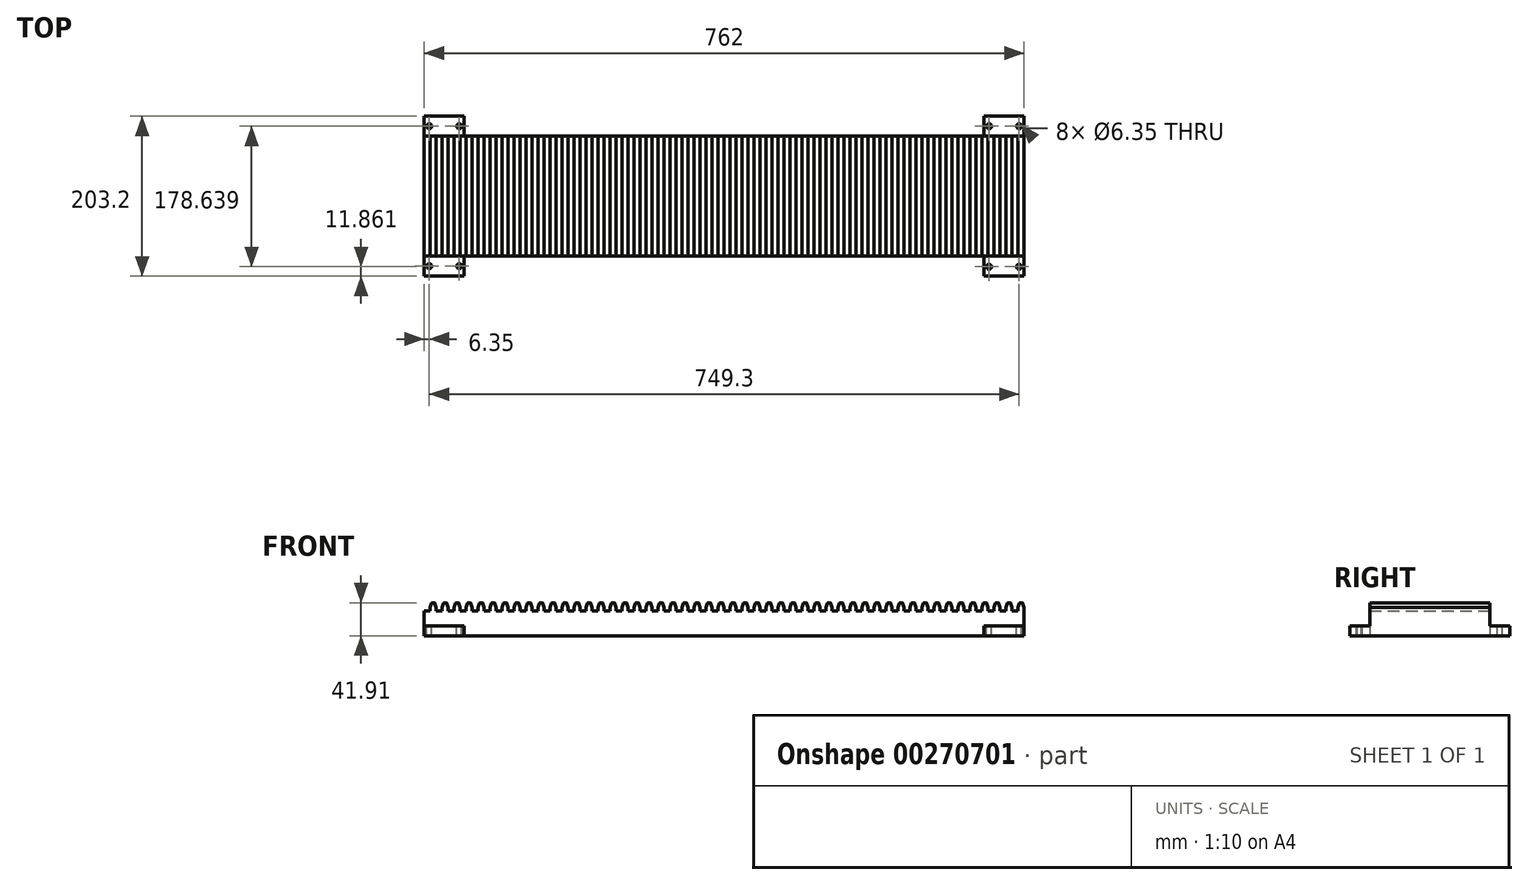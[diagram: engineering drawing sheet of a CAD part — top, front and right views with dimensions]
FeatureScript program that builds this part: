
annotation { "Feature Type Name" : "Feature", "Feature Type Description" : "" }
export const myFeature = defineFeature(function(context is Context, id is Id, definition is map)
    precondition{}
    {
        {
            var Q0;
            Q0=qCreatedBy(makeId("Front.planeOp"),FACE);
            var sketch = newSketch(context, id + "F0", { "sketchPlane" : qUnion([Q0])});
            skLineSegment(sketch, "E0.bottom", {"start": v(0, 0) * mm, "end": v(762, 0) * mm});
            skLineSegment(sketch, "E0.top", {"start": v(0, 31.75) * mm, "end": v(762, 31.75) * mm});
            skLineSegment(sketch, "E0.left", {"start": v(0, 0) * mm, "end": v(0, 31.75) * mm});
            skLineSegment(sketch, "E0.right", {"start": v(762, 0) * mm, "end": v(762, 31.75) * mm});
            skPoint(sketch, "E1.centerSnap0", {"position": v(11.43, 41.91) * mm});
            skPoint(sketch, "E2", {"position": v(7.62, 35.71) * mm});
            skPoint(sketch, "E3", {"position": v(15.24, 35.71) * mm});
            skLineSegment(sketch, "E4", {"start": v(7.62, 31.75) * mm, "end": v(7.62, 35.71) * mm});
            skPoint(sketch, "E5", {"position": v(7.62, 41.91) * mm});
            skLineSegment(sketch, "E6", {"start": v(15.24, 35.71) * mm, "end": v(15.24, 31.75) * mm});
            skLineSegment(sketch, "E7", {"start": v(10, 41.91) * mm, "end": v(11.43, 41.91) * mm});
            skLineSegment(sketch, "E8", {"start": v(12.87, 41.91) * mm, "end": v(11.43, 41.91) * mm});
            skLineSegment(sketch, "E9", {"start": v(7.62, 35.71) * mm, "end": v(9.39, 41.46) * mm});
            skLineSegment(sketch, "E10", {"start": v(15.24, 35.71) * mm, "end": v(13.47, 41.46) * mm});
            skPoint(sketch, "E11.start.orphan", {"position": v(15.24, 41.91) * mm});
            skPoint(sketch, "E12.visualSharp", {"position": v(9.52, 41.91) * mm});
            skArc(sketch, "E12.filletArc", {"start": v(10, 41.91) * mm, "mid": v(9.62, 41.79) * mm, "end": v(9.39, 41.46) * mm});
            skPoint(sketch, "E13.visualSharp", {"position": v(13.33, 41.91) * mm});
            skArc(sketch, "E13.filletArc", {"start": v(13.47, 41.46) * mm, "mid": v(13.24, 41.79) * mm, "end": v(12.87, 41.91) * mm});
            skLineSegment(sketch, "E14.1.0.0", {"start": v(22.86, 31.75) * mm, "end": v(22.86, 35.71) * mm});
            skLineSegment(sketch, "E14.1.0.1", {"start": v(22.86, 35.71) * mm, "end": v(24.63, 41.46) * mm});
            skArc(sketch, "E14.1.0.2", {"start": v(25.23, 41.91) * mm, "mid": v(24.86, 41.79) * mm, "end": v(24.63, 41.46) * mm});
            skLineSegment(sketch, "E14.1.0.3", {"start": v(25.23, 41.91) * mm, "end": v(26.67, 41.91) * mm});
            skLineSegment(sketch, "E14.1.0.4", {"start": v(28.1, 41.91) * mm, "end": v(26.67, 41.91) * mm});
            skArc(sketch, "E14.1.0.5", {"start": v(28.71, 41.46) * mm, "mid": v(28.48, 41.79) * mm, "end": v(28.1, 41.91) * mm});
            skLineSegment(sketch, "E14.1.0.6", {"start": v(30.48, 35.71) * mm, "end": v(28.71, 41.46) * mm});
            skLineSegment(sketch, "E14.1.0.7", {"start": v(30.48, 35.71) * mm, "end": v(30.48, 31.75) * mm});
            skLineSegment(sketch, "E14.2.0.0", {"start": v(38.1, 31.75) * mm, "end": v(38.1, 35.71) * mm});
            skLineSegment(sketch, "E14.2.0.1", {"start": v(38.1, 35.71) * mm, "end": v(39.87, 41.46) * mm});
            skArc(sketch, "E14.2.0.2", {"start": v(40.47, 41.91) * mm, "mid": v(40.1, 41.79) * mm, "end": v(39.87, 41.46) * mm});
            skLineSegment(sketch, "E14.2.0.3", {"start": v(40.47, 41.91) * mm, "end": v(41.9, 41.91) * mm});
            skLineSegment(sketch, "E14.2.0.4", {"start": v(43.35, 41.91) * mm, "end": v(41.9, 41.91) * mm});
            skArc(sketch, "E14.2.0.5", {"start": v(43.95, 41.46) * mm, "mid": v(43.72, 41.79) * mm, "end": v(43.35, 41.91) * mm});
            skLineSegment(sketch, "E14.2.0.6", {"start": v(45.72, 35.71) * mm, "end": v(43.95, 41.46) * mm});
            skLineSegment(sketch, "E14.2.0.7", {"start": v(45.72, 35.71) * mm, "end": v(45.72, 31.75) * mm});
            skLineSegment(sketch, "E14.3.0.0", {"start": v(53.34, 31.75) * mm, "end": v(53.34, 35.71) * mm});
            skLineSegment(sketch, "E14.3.0.1", {"start": v(53.34, 35.71) * mm, "end": v(55.1, 41.46) * mm});
            skArc(sketch, "E14.3.0.2", {"start": v(55.71, 41.91) * mm, "mid": v(55.34, 41.79) * mm, "end": v(55.1, 41.46) * mm});
            skLineSegment(sketch, "E14.3.0.3", {"start": v(55.71, 41.91) * mm, "end": v(57.15, 41.91) * mm});
            skLineSegment(sketch, "E14.3.0.4", {"start": v(58.59, 41.91) * mm, "end": v(57.15, 41.91) * mm});
            skArc(sketch, "E14.3.0.5", {"start": v(59.2, 41.46) * mm, "mid": v(58.96, 41.79) * mm, "end": v(58.59, 41.91) * mm});
            skLineSegment(sketch, "E14.3.0.6", {"start": v(60.96, 35.71) * mm, "end": v(59.2, 41.46) * mm});
            skLineSegment(sketch, "E14.3.0.7", {"start": v(60.96, 35.71) * mm, "end": v(60.96, 31.75) * mm});
            skLineSegment(sketch, "E14.4.0.0", {"start": v(68.58, 31.75) * mm, "end": v(68.58, 35.71) * mm});
            skLineSegment(sketch, "E14.4.0.1", {"start": v(68.58, 35.71) * mm, "end": v(70.35, 41.46) * mm});
            skArc(sketch, "E14.4.0.2", {"start": v(70.95, 41.91) * mm, "mid": v(70.58, 41.79) * mm, "end": v(70.35, 41.46) * mm});
            skLineSegment(sketch, "E14.4.0.3", {"start": v(70.95, 41.91) * mm, "end": v(72.39, 41.91) * mm});
            skLineSegment(sketch, "E14.4.0.4", {"start": v(73.83, 41.91) * mm, "end": v(72.39, 41.91) * mm});
            skArc(sketch, "E14.4.0.5", {"start": v(74.43, 41.46) * mm, "mid": v(74.2, 41.79) * mm, "end": v(73.83, 41.91) * mm});
            skLineSegment(sketch, "E14.4.0.6", {"start": v(76.2, 35.71) * mm, "end": v(74.43, 41.46) * mm});
            skLineSegment(sketch, "E14.4.0.7", {"start": v(76.2, 35.71) * mm, "end": v(76.2, 31.75) * mm});
            skLineSegment(sketch, "E14.5.0.0", {"start": v(83.82, 31.75) * mm, "end": v(83.82, 35.71) * mm});
            skLineSegment(sketch, "E14.5.0.1", {"start": v(83.82, 35.71) * mm, "end": v(85.59, 41.46) * mm});
            skArc(sketch, "E14.5.0.2", {"start": v(86.2, 41.91) * mm, "mid": v(85.82, 41.79) * mm, "end": v(85.59, 41.46) * mm});
            skLineSegment(sketch, "E14.5.0.3", {"start": v(86.2, 41.91) * mm, "end": v(87.63, 41.91) * mm});
            skLineSegment(sketch, "E14.5.0.4", {"start": v(89.07, 41.91) * mm, "end": v(87.63, 41.91) * mm});
            skArc(sketch, "E14.5.0.5", {"start": v(89.67, 41.46) * mm, "mid": v(89.44, 41.79) * mm, "end": v(89.07, 41.91) * mm});
            skLineSegment(sketch, "E14.5.0.6", {"start": v(91.44, 35.71) * mm, "end": v(89.67, 41.46) * mm});
            skLineSegment(sketch, "E14.5.0.7", {"start": v(91.44, 35.71) * mm, "end": v(91.44, 31.75) * mm});
            skLineSegment(sketch, "E14.6.0.0", {"start": v(99.06, 31.75) * mm, "end": v(99.06, 35.71) * mm});
            skLineSegment(sketch, "E14.6.0.1", {"start": v(99.06, 35.71) * mm, "end": v(100.83, 41.46) * mm});
            skArc(sketch, "E14.6.0.2", {"start": v(101.43, 41.91) * mm, "mid": v(101.06, 41.79) * mm, "end": v(100.83, 41.46) * mm});
            skLineSegment(sketch, "E14.6.0.3", {"start": v(101.43, 41.91) * mm, "end": v(102.87, 41.91) * mm});
            skLineSegment(sketch, "E14.6.0.4", {"start": v(104.3, 41.91) * mm, "end": v(102.87, 41.91) * mm});
            skArc(sketch, "E14.6.0.5", {"start": v(104.91, 41.46) * mm, "mid": v(104.68, 41.79) * mm, "end": v(104.3, 41.91) * mm});
            skLineSegment(sketch, "E14.6.0.6", {"start": v(106.68, 35.71) * mm, "end": v(104.91, 41.46) * mm});
            skLineSegment(sketch, "E14.6.0.7", {"start": v(106.68, 35.71) * mm, "end": v(106.68, 31.75) * mm});
            skLineSegment(sketch, "E14.7.0.0", {"start": v(114.3, 31.75) * mm, "end": v(114.3, 35.71) * mm});
            skLineSegment(sketch, "E14.7.0.1", {"start": v(114.3, 35.71) * mm, "end": v(116.07, 41.46) * mm});
            skArc(sketch, "E14.7.0.2", {"start": v(116.67, 41.91) * mm, "mid": v(116.3, 41.79) * mm, "end": v(116.07, 41.46) * mm});
            skLineSegment(sketch, "E14.7.0.3", {"start": v(116.67, 41.91) * mm, "end": v(118.11, 41.91) * mm});
            skLineSegment(sketch, "E14.7.0.4", {"start": v(119.55, 41.91) * mm, "end": v(118.1, 41.91) * mm});
            skArc(sketch, "E14.7.0.5", {"start": v(120.15, 41.46) * mm, "mid": v(119.92, 41.79) * mm, "end": v(119.55, 41.91) * mm});
            skLineSegment(sketch, "E14.7.0.6", {"start": v(121.92, 35.71) * mm, "end": v(120.15, 41.46) * mm});
            skLineSegment(sketch, "E14.7.0.7", {"start": v(121.92, 35.71) * mm, "end": v(121.92, 31.75) * mm});
            skLineSegment(sketch, "E14.8.0.0", {"start": v(129.54, 31.75) * mm, "end": v(129.54, 35.71) * mm});
            skLineSegment(sketch, "E14.8.0.1", {"start": v(129.54, 35.71) * mm, "end": v(131.3, 41.46) * mm});
            skArc(sketch, "E14.8.0.2", {"start": v(131.91, 41.91) * mm, "mid": v(131.54, 41.79) * mm, "end": v(131.3, 41.46) * mm});
            skLineSegment(sketch, "E14.8.0.3", {"start": v(131.91, 41.91) * mm, "end": v(133.35, 41.91) * mm});
            skLineSegment(sketch, "E14.8.0.4", {"start": v(134.79, 41.91) * mm, "end": v(133.35, 41.91) * mm});
            skArc(sketch, "E14.8.0.5", {"start": v(135.4, 41.46) * mm, "mid": v(135.16, 41.79) * mm, "end": v(134.79, 41.91) * mm});
            skLineSegment(sketch, "E14.8.0.6", {"start": v(137.16, 35.71) * mm, "end": v(135.4, 41.46) * mm});
            skLineSegment(sketch, "E14.8.0.7", {"start": v(137.16, 35.71) * mm, "end": v(137.16, 31.75) * mm});
            skLineSegment(sketch, "E14.9.0.0", {"start": v(144.78, 31.75) * mm, "end": v(144.78, 35.71) * mm});
            skLineSegment(sketch, "E14.9.0.1", {"start": v(144.78, 35.71) * mm, "end": v(146.55, 41.46) * mm});
            skArc(sketch, "E14.9.0.2", {"start": v(147.15, 41.91) * mm, "mid": v(146.78, 41.79) * mm, "end": v(146.55, 41.46) * mm});
            skLineSegment(sketch, "E14.9.0.3", {"start": v(147.15, 41.91) * mm, "end": v(148.6, 41.91) * mm});
            skLineSegment(sketch, "E14.9.0.4", {"start": v(150.03, 41.91) * mm, "end": v(148.6, 41.91) * mm});
            skArc(sketch, "E14.9.0.5", {"start": v(150.63, 41.46) * mm, "mid": v(150.4, 41.79) * mm, "end": v(150.03, 41.91) * mm});
            skLineSegment(sketch, "E14.9.0.6", {"start": v(152.4, 35.71) * mm, "end": v(150.63, 41.46) * mm});
            skLineSegment(sketch, "E14.9.0.7", {"start": v(152.4, 35.71) * mm, "end": v(152.4, 31.75) * mm});
            skLineSegment(sketch, "E14.10.0.0", {"start": v(160.02, 31.75) * mm, "end": v(160.02, 35.71) * mm});
            skLineSegment(sketch, "E14.10.0.1", {"start": v(160.02, 35.71) * mm, "end": v(161.79, 41.46) * mm});
            skArc(sketch, "E14.10.0.2", {"start": v(162.4, 41.91) * mm, "mid": v(162.02, 41.79) * mm, "end": v(161.79, 41.46) * mm});
            skLineSegment(sketch, "E14.10.0.3", {"start": v(162.4, 41.91) * mm, "end": v(163.83, 41.91) * mm});
            skLineSegment(sketch, "E14.10.0.4", {"start": v(165.27, 41.91) * mm, "end": v(163.83, 41.91) * mm});
            skArc(sketch, "E14.10.0.5", {"start": v(165.87, 41.46) * mm, "mid": v(165.64, 41.79) * mm, "end": v(165.27, 41.91) * mm});
            skLineSegment(sketch, "E14.10.0.6", {"start": v(167.64, 35.71) * mm, "end": v(165.87, 41.46) * mm});
            skLineSegment(sketch, "E14.10.0.7", {"start": v(167.64, 35.71) * mm, "end": v(167.64, 31.75) * mm});
            skLineSegment(sketch, "E14.11.0.0", {"start": v(175.26, 31.75) * mm, "end": v(175.26, 35.71) * mm});
            skLineSegment(sketch, "E14.11.0.1", {"start": v(175.26, 35.71) * mm, "end": v(177.03, 41.46) * mm});
            skArc(sketch, "E14.11.0.2", {"start": v(177.63, 41.91) * mm, "mid": v(177.26, 41.79) * mm, "end": v(177.03, 41.46) * mm});
            skLineSegment(sketch, "E14.11.0.3", {"start": v(177.63, 41.91) * mm, "end": v(179.07, 41.91) * mm});
            skLineSegment(sketch, "E14.11.0.4", {"start": v(180.5, 41.91) * mm, "end": v(179.07, 41.91) * mm});
            skArc(sketch, "E14.11.0.5", {"start": v(181.11, 41.46) * mm, "mid": v(180.88, 41.79) * mm, "end": v(180.5, 41.91) * mm});
            skLineSegment(sketch, "E14.11.0.6", {"start": v(182.88, 35.71) * mm, "end": v(181.11, 41.46) * mm});
            skLineSegment(sketch, "E14.11.0.7", {"start": v(182.88, 35.71) * mm, "end": v(182.88, 31.75) * mm});
            skLineSegment(sketch, "E14.12.0.0", {"start": v(190.5, 31.75) * mm, "end": v(190.5, 35.71) * mm});
            skLineSegment(sketch, "E14.12.0.1", {"start": v(190.5, 35.71) * mm, "end": v(192.27, 41.46) * mm});
            skArc(sketch, "E14.12.0.2", {"start": v(192.87, 41.91) * mm, "mid": v(192.5, 41.79) * mm, "end": v(192.27, 41.46) * mm});
            skLineSegment(sketch, "E14.12.0.3", {"start": v(192.87, 41.91) * mm, "end": v(194.3, 41.91) * mm});
            skLineSegment(sketch, "E14.12.0.4", {"start": v(195.75, 41.91) * mm, "end": v(194.3, 41.91) * mm});
            skArc(sketch, "E14.12.0.5", {"start": v(196.35, 41.46) * mm, "mid": v(196.12, 41.79) * mm, "end": v(195.75, 41.91) * mm});
            skLineSegment(sketch, "E14.12.0.6", {"start": v(198.12, 35.71) * mm, "end": v(196.35, 41.46) * mm});
            skLineSegment(sketch, "E14.12.0.7", {"start": v(198.12, 35.71) * mm, "end": v(198.12, 31.75) * mm});
            skLineSegment(sketch, "E14.13.0.0", {"start": v(205.74, 31.75) * mm, "end": v(205.74, 35.71) * mm});
            skLineSegment(sketch, "E14.13.0.1", {"start": v(205.74, 35.71) * mm, "end": v(207.5, 41.46) * mm});
            skArc(sketch, "E14.13.0.2", {"start": v(208.11, 41.91) * mm, "mid": v(207.74, 41.79) * mm, "end": v(207.5, 41.46) * mm});
            skLineSegment(sketch, "E14.13.0.3", {"start": v(208.11, 41.91) * mm, "end": v(209.55, 41.91) * mm});
            skLineSegment(sketch, "E14.13.0.4", {"start": v(210.99, 41.91) * mm, "end": v(209.55, 41.91) * mm});
            skArc(sketch, "E14.13.0.5", {"start": v(211.6, 41.46) * mm, "mid": v(211.36, 41.79) * mm, "end": v(210.99, 41.91) * mm});
            skLineSegment(sketch, "E14.13.0.6", {"start": v(213.36, 35.71) * mm, "end": v(211.6, 41.46) * mm});
            skLineSegment(sketch, "E14.13.0.7", {"start": v(213.36, 35.71) * mm, "end": v(213.36, 31.75) * mm});
            skLineSegment(sketch, "E14.14.0.0", {"start": v(220.98, 31.75) * mm, "end": v(220.98, 35.71) * mm});
            skLineSegment(sketch, "E14.14.0.1", {"start": v(220.98, 35.71) * mm, "end": v(222.75, 41.46) * mm});
            skArc(sketch, "E14.14.0.2", {"start": v(223.35, 41.91) * mm, "mid": v(222.98, 41.79) * mm, "end": v(222.75, 41.46) * mm});
            skLineSegment(sketch, "E14.14.0.3", {"start": v(223.35, 41.91) * mm, "end": v(224.79, 41.91) * mm});
            skLineSegment(sketch, "E14.14.0.4", {"start": v(226.23, 41.91) * mm, "end": v(224.79, 41.91) * mm});
            skArc(sketch, "E14.14.0.5", {"start": v(226.83, 41.46) * mm, "mid": v(226.6, 41.79) * mm, "end": v(226.23, 41.91) * mm});
            skLineSegment(sketch, "E14.14.0.6", {"start": v(228.6, 35.71) * mm, "end": v(226.83, 41.46) * mm});
            skLineSegment(sketch, "E14.14.0.7", {"start": v(228.6, 35.71) * mm, "end": v(228.6, 31.75) * mm});
            skLineSegment(sketch, "E14.15.0.0", {"start": v(236.22, 31.75) * mm, "end": v(236.22, 35.71) * mm});
            skLineSegment(sketch, "E14.15.0.1", {"start": v(236.22, 35.71) * mm, "end": v(237.99, 41.46) * mm});
            skArc(sketch, "E14.15.0.2", {"start": v(238.6, 41.91) * mm, "mid": v(238.22, 41.79) * mm, "end": v(237.99, 41.46) * mm});
            skLineSegment(sketch, "E14.15.0.3", {"start": v(238.6, 41.91) * mm, "end": v(240.03, 41.91) * mm});
            skLineSegment(sketch, "E14.15.0.4", {"start": v(241.47, 41.91) * mm, "end": v(240.03, 41.91) * mm});
            skArc(sketch, "E14.15.0.5", {"start": v(242.07, 41.46) * mm, "mid": v(241.84, 41.79) * mm, "end": v(241.47, 41.91) * mm});
            skLineSegment(sketch, "E14.15.0.6", {"start": v(243.84, 35.71) * mm, "end": v(242.07, 41.46) * mm});
            skLineSegment(sketch, "E14.15.0.7", {"start": v(243.84, 35.71) * mm, "end": v(243.84, 31.75) * mm});
            skLineSegment(sketch, "E14.16.0.0", {"start": v(251.46, 31.75) * mm, "end": v(251.46, 35.71) * mm});
            skLineSegment(sketch, "E14.16.0.1", {"start": v(251.46, 35.71) * mm, "end": v(253.23, 41.46) * mm});
            skArc(sketch, "E14.16.0.2", {"start": v(253.83, 41.91) * mm, "mid": v(253.46, 41.79) * mm, "end": v(253.23, 41.46) * mm});
            skLineSegment(sketch, "E14.16.0.3", {"start": v(253.83, 41.91) * mm, "end": v(255.27, 41.91) * mm});
            skLineSegment(sketch, "E14.16.0.4", {"start": v(256.7, 41.91) * mm, "end": v(255.27, 41.91) * mm});
            skArc(sketch, "E14.16.0.5", {"start": v(257.31, 41.46) * mm, "mid": v(257.08, 41.79) * mm, "end": v(256.7, 41.91) * mm});
            skLineSegment(sketch, "E14.16.0.6", {"start": v(259.08, 35.71) * mm, "end": v(257.31, 41.46) * mm});
            skLineSegment(sketch, "E14.16.0.7", {"start": v(259.08, 35.71) * mm, "end": v(259.08, 31.75) * mm});
            skLineSegment(sketch, "E14.17.0.0", {"start": v(266.7, 31.75) * mm, "end": v(266.7, 35.71) * mm});
            skLineSegment(sketch, "E14.17.0.1", {"start": v(266.7, 35.71) * mm, "end": v(268.47, 41.46) * mm});
            skArc(sketch, "E14.17.0.2", {"start": v(269.07, 41.91) * mm, "mid": v(268.7, 41.79) * mm, "end": v(268.47, 41.46) * mm});
            skLineSegment(sketch, "E14.17.0.3", {"start": v(269.07, 41.91) * mm, "end": v(270.5, 41.91) * mm});
            skLineSegment(sketch, "E14.17.0.4", {"start": v(271.95, 41.91) * mm, "end": v(270.5, 41.91) * mm});
            skArc(sketch, "E14.17.0.5", {"start": v(272.55, 41.46) * mm, "mid": v(272.32, 41.79) * mm, "end": v(271.95, 41.91) * mm});
            skLineSegment(sketch, "E14.17.0.6", {"start": v(274.32, 35.71) * mm, "end": v(272.55, 41.46) * mm});
            skLineSegment(sketch, "E14.17.0.7", {"start": v(274.32, 35.71) * mm, "end": v(274.32, 31.75) * mm});
            skLineSegment(sketch, "E14.18.0.0", {"start": v(281.94, 31.75) * mm, "end": v(281.94, 35.71) * mm});
            skLineSegment(sketch, "E14.18.0.1", {"start": v(281.94, 35.71) * mm, "end": v(283.7, 41.46) * mm});
            skArc(sketch, "E14.18.0.2", {"start": v(284.31, 41.91) * mm, "mid": v(283.94, 41.79) * mm, "end": v(283.7, 41.46) * mm});
            skLineSegment(sketch, "E14.18.0.3", {"start": v(284.31, 41.91) * mm, "end": v(285.75, 41.91) * mm});
            skLineSegment(sketch, "E14.18.0.4", {"start": v(287.19, 41.91) * mm, "end": v(285.75, 41.91) * mm});
            skArc(sketch, "E14.18.0.5", {"start": v(287.8, 41.46) * mm, "mid": v(287.56, 41.79) * mm, "end": v(287.19, 41.91) * mm});
            skLineSegment(sketch, "E14.18.0.6", {"start": v(289.56, 35.71) * mm, "end": v(287.8, 41.46) * mm});
            skLineSegment(sketch, "E14.18.0.7", {"start": v(289.56, 35.71) * mm, "end": v(289.56, 31.75) * mm});
            skLineSegment(sketch, "E14.19.0.0", {"start": v(297.18, 31.75) * mm, "end": v(297.18, 35.71) * mm});
            skLineSegment(sketch, "E14.19.0.1", {"start": v(297.18, 35.71) * mm, "end": v(298.95, 41.46) * mm});
            skArc(sketch, "E14.19.0.2", {"start": v(299.55, 41.91) * mm, "mid": v(299.18, 41.79) * mm, "end": v(298.95, 41.46) * mm});
            skLineSegment(sketch, "E14.19.0.3", {"start": v(299.55, 41.91) * mm, "end": v(300.99, 41.91) * mm});
            skLineSegment(sketch, "E14.19.0.4", {"start": v(302.43, 41.91) * mm, "end": v(300.99, 41.91) * mm});
            skArc(sketch, "E14.19.0.5", {"start": v(303.03, 41.46) * mm, "mid": v(302.8, 41.79) * mm, "end": v(302.43, 41.91) * mm});
            skLineSegment(sketch, "E14.19.0.6", {"start": v(304.8, 35.71) * mm, "end": v(303.03, 41.46) * mm});
            skLineSegment(sketch, "E14.19.0.7", {"start": v(304.8, 35.71) * mm, "end": v(304.8, 31.75) * mm});
            skLineSegment(sketch, "E14.20.0.0", {"start": v(312.42, 31.75) * mm, "end": v(312.42, 35.71) * mm});
            skLineSegment(sketch, "E14.20.0.1", {"start": v(312.42, 35.71) * mm, "end": v(314.19, 41.46) * mm});
            skArc(sketch, "E14.20.0.2", {"start": v(314.8, 41.91) * mm, "mid": v(314.42, 41.79) * mm, "end": v(314.19, 41.46) * mm});
            skLineSegment(sketch, "E14.20.0.3", {"start": v(314.8, 41.91) * mm, "end": v(316.23, 41.91) * mm});
            skLineSegment(sketch, "E14.20.0.4", {"start": v(317.67, 41.91) * mm, "end": v(316.23, 41.91) * mm});
            skArc(sketch, "E14.20.0.5", {"start": v(318.27, 41.46) * mm, "mid": v(318.04, 41.79) * mm, "end": v(317.67, 41.91) * mm});
            skLineSegment(sketch, "E14.20.0.6", {"start": v(320.04, 35.71) * mm, "end": v(318.27, 41.46) * mm});
            skLineSegment(sketch, "E14.20.0.7", {"start": v(320.04, 35.71) * mm, "end": v(320.04, 31.75) * mm});
            skLineSegment(sketch, "E14.21.0.0", {"start": v(327.66, 31.75) * mm, "end": v(327.66, 35.71) * mm});
            skLineSegment(sketch, "E14.21.0.1", {"start": v(327.66, 35.71) * mm, "end": v(329.43, 41.46) * mm});
            skArc(sketch, "E14.21.0.2", {"start": v(330.03, 41.91) * mm, "mid": v(329.66, 41.79) * mm, "end": v(329.43, 41.46) * mm});
            skLineSegment(sketch, "E14.21.0.3", {"start": v(330.03, 41.91) * mm, "end": v(331.47, 41.91) * mm});
            skLineSegment(sketch, "E14.21.0.4", {"start": v(332.9, 41.91) * mm, "end": v(331.47, 41.91) * mm});
            skArc(sketch, "E14.21.0.5", {"start": v(333.51, 41.46) * mm, "mid": v(333.28, 41.79) * mm, "end": v(332.9, 41.91) * mm});
            skLineSegment(sketch, "E14.21.0.6", {"start": v(335.28, 35.71) * mm, "end": v(333.51, 41.46) * mm});
            skLineSegment(sketch, "E14.21.0.7", {"start": v(335.28, 35.71) * mm, "end": v(335.28, 31.75) * mm});
            skLineSegment(sketch, "E14.22.0.0", {"start": v(342.9, 31.75) * mm, "end": v(342.9, 35.71) * mm});
            skLineSegment(sketch, "E14.22.0.1", {"start": v(342.9, 35.71) * mm, "end": v(344.67, 41.46) * mm});
            skArc(sketch, "E14.22.0.2", {"start": v(345.27, 41.91) * mm, "mid": v(344.9, 41.79) * mm, "end": v(344.67, 41.46) * mm});
            skLineSegment(sketch, "E14.22.0.3", {"start": v(345.27, 41.91) * mm, "end": v(346.71, 41.91) * mm});
            skLineSegment(sketch, "E14.22.0.4", {"start": v(348.15, 41.91) * mm, "end": v(346.71, 41.91) * mm});
            skArc(sketch, "E14.22.0.5", {"start": v(348.75, 41.46) * mm, "mid": v(348.52, 41.79) * mm, "end": v(348.15, 41.91) * mm});
            skLineSegment(sketch, "E14.22.0.6", {"start": v(350.52, 35.71) * mm, "end": v(348.75, 41.46) * mm});
            skLineSegment(sketch, "E14.22.0.7", {"start": v(350.52, 35.71) * mm, "end": v(350.52, 31.75) * mm});
            skLineSegment(sketch, "E14.23.0.0", {"start": v(358.14, 31.75) * mm, "end": v(358.14, 35.71) * mm});
            skLineSegment(sketch, "E14.23.0.1", {"start": v(358.14, 35.71) * mm, "end": v(359.9, 41.46) * mm});
            skArc(sketch, "E14.23.0.2", {"start": v(360.51, 41.91) * mm, "mid": v(360.14, 41.79) * mm, "end": v(359.9, 41.46) * mm});
            skLineSegment(sketch, "E14.23.0.3", {"start": v(360.51, 41.91) * mm, "end": v(361.95, 41.91) * mm});
            skLineSegment(sketch, "E14.23.0.4", {"start": v(363.39, 41.91) * mm, "end": v(361.95, 41.91) * mm});
            skArc(sketch, "E14.23.0.5", {"start": v(364, 41.46) * mm, "mid": v(363.76, 41.79) * mm, "end": v(363.39, 41.91) * mm});
            skLineSegment(sketch, "E14.23.0.6", {"start": v(365.76, 35.71) * mm, "end": v(364, 41.46) * mm});
            skLineSegment(sketch, "E14.23.0.7", {"start": v(365.76, 35.71) * mm, "end": v(365.76, 31.75) * mm});
            skLineSegment(sketch, "E14.24.0.0", {"start": v(373.38, 31.75) * mm, "end": v(373.38, 35.71) * mm});
            skLineSegment(sketch, "E14.24.0.1", {"start": v(373.38, 35.71) * mm, "end": v(375.15, 41.46) * mm});
            skArc(sketch, "E14.24.0.2", {"start": v(375.75, 41.91) * mm, "mid": v(375.38, 41.79) * mm, "end": v(375.15, 41.46) * mm});
            skLineSegment(sketch, "E14.24.0.3", {"start": v(375.75, 41.91) * mm, "end": v(377.2, 41.91) * mm});
            skLineSegment(sketch, "E14.24.0.4", {"start": v(378.63, 41.91) * mm, "end": v(377.2, 41.91) * mm});
            skArc(sketch, "E14.24.0.5", {"start": v(379.23, 41.46) * mm, "mid": v(379, 41.79) * mm, "end": v(378.63, 41.91) * mm});
            skLineSegment(sketch, "E14.24.0.6", {"start": v(381, 35.71) * mm, "end": v(379.23, 41.46) * mm});
            skLineSegment(sketch, "E14.24.0.7", {"start": v(381, 35.71) * mm, "end": v(381, 31.75) * mm});
            skLineSegment(sketch, "E14.25.0.0", {"start": v(388.62, 31.75) * mm, "end": v(388.62, 35.71) * mm});
            skLineSegment(sketch, "E14.25.0.1", {"start": v(388.62, 35.71) * mm, "end": v(390.39, 41.46) * mm});
            skArc(sketch, "E14.25.0.2", {"start": v(391, 41.91) * mm, "mid": v(390.62, 41.79) * mm, "end": v(390.39, 41.46) * mm});
            skLineSegment(sketch, "E14.25.0.3", {"start": v(391, 41.91) * mm, "end": v(392.43, 41.91) * mm});
            skLineSegment(sketch, "E14.25.0.4", {"start": v(393.87, 41.91) * mm, "end": v(392.43, 41.91) * mm});
            skArc(sketch, "E14.25.0.5", {"start": v(394.47, 41.46) * mm, "mid": v(394.24, 41.79) * mm, "end": v(393.87, 41.91) * mm});
            skLineSegment(sketch, "E14.25.0.6", {"start": v(396.24, 35.71) * mm, "end": v(394.47, 41.46) * mm});
            skLineSegment(sketch, "E14.25.0.7", {"start": v(396.24, 35.71) * mm, "end": v(396.24, 31.75) * mm});
            skLineSegment(sketch, "E14.26.0.0", {"start": v(403.86, 31.75) * mm, "end": v(403.86, 35.71) * mm});
            skLineSegment(sketch, "E14.26.0.1", {"start": v(403.86, 35.71) * mm, "end": v(405.63, 41.46) * mm});
            skArc(sketch, "E14.26.0.2", {"start": v(406.23, 41.91) * mm, "mid": v(405.86, 41.79) * mm, "end": v(405.63, 41.46) * mm});
            skLineSegment(sketch, "E14.26.0.3", {"start": v(406.23, 41.91) * mm, "end": v(407.67, 41.91) * mm});
            skLineSegment(sketch, "E14.26.0.4", {"start": v(409.1, 41.91) * mm, "end": v(407.67, 41.91) * mm});
            skArc(sketch, "E14.26.0.5", {"start": v(409.71, 41.46) * mm, "mid": v(409.48, 41.79) * mm, "end": v(409.1, 41.91) * mm});
            skLineSegment(sketch, "E14.26.0.6", {"start": v(411.48, 35.71) * mm, "end": v(409.71, 41.46) * mm});
            skLineSegment(sketch, "E14.26.0.7", {"start": v(411.48, 35.71) * mm, "end": v(411.48, 31.75) * mm});
            skLineSegment(sketch, "E14.27.0.0", {"start": v(419.1, 31.75) * mm, "end": v(419.1, 35.71) * mm});
            skLineSegment(sketch, "E14.27.0.1", {"start": v(419.1, 35.71) * mm, "end": v(420.87, 41.46) * mm});
            skArc(sketch, "E14.27.0.2", {"start": v(421.47, 41.91) * mm, "mid": v(421.1, 41.79) * mm, "end": v(420.87, 41.46) * mm});
            skLineSegment(sketch, "E14.27.0.3", {"start": v(421.47, 41.91) * mm, "end": v(422.91, 41.91) * mm});
            skLineSegment(sketch, "E14.27.0.4", {"start": v(424.35, 41.91) * mm, "end": v(422.91, 41.91) * mm});
            skArc(sketch, "E14.27.0.5", {"start": v(424.95, 41.46) * mm, "mid": v(424.72, 41.79) * mm, "end": v(424.35, 41.91) * mm});
            skLineSegment(sketch, "E14.27.0.6", {"start": v(426.72, 35.71) * mm, "end": v(424.95, 41.46) * mm});
            skLineSegment(sketch, "E14.27.0.7", {"start": v(426.72, 35.71) * mm, "end": v(426.72, 31.75) * mm});
            skLineSegment(sketch, "E14.28.0.0", {"start": v(434.34, 31.75) * mm, "end": v(434.34, 35.71) * mm});
            skLineSegment(sketch, "E14.28.0.1", {"start": v(434.34, 35.71) * mm, "end": v(436.1, 41.46) * mm});
            skArc(sketch, "E14.28.0.2", {"start": v(436.71, 41.91) * mm, "mid": v(436.34, 41.79) * mm, "end": v(436.1, 41.46) * mm});
            skLineSegment(sketch, "E14.28.0.3", {"start": v(436.71, 41.91) * mm, "end": v(438.15, 41.91) * mm});
            skLineSegment(sketch, "E14.28.0.4", {"start": v(439.59, 41.91) * mm, "end": v(438.15, 41.91) * mm});
            skArc(sketch, "E14.28.0.5", {"start": v(440.2, 41.46) * mm, "mid": v(439.96, 41.79) * mm, "end": v(439.59, 41.91) * mm});
            skLineSegment(sketch, "E14.28.0.6", {"start": v(441.96, 35.71) * mm, "end": v(440.2, 41.46) * mm});
            skLineSegment(sketch, "E14.28.0.7", {"start": v(441.96, 35.71) * mm, "end": v(441.96, 31.75) * mm});
            skLineSegment(sketch, "E14.29.0.0", {"start": v(449.58, 31.75) * mm, "end": v(449.58, 35.71) * mm});
            skLineSegment(sketch, "E14.29.0.1", {"start": v(449.58, 35.71) * mm, "end": v(451.35, 41.46) * mm});
            skArc(sketch, "E14.29.0.2", {"start": v(451.95, 41.91) * mm, "mid": v(451.58, 41.79) * mm, "end": v(451.35, 41.46) * mm});
            skLineSegment(sketch, "E14.29.0.3", {"start": v(451.95, 41.91) * mm, "end": v(453.4, 41.91) * mm});
            skLineSegment(sketch, "E14.29.0.4", {"start": v(454.83, 41.91) * mm, "end": v(453.4, 41.91) * mm});
            skArc(sketch, "E14.29.0.5", {"start": v(455.43, 41.46) * mm, "mid": v(455.2, 41.79) * mm, "end": v(454.83, 41.91) * mm});
            skLineSegment(sketch, "E14.29.0.6", {"start": v(457.2, 35.71) * mm, "end": v(455.43, 41.46) * mm});
            skLineSegment(sketch, "E14.29.0.7", {"start": v(457.2, 35.71) * mm, "end": v(457.2, 31.75) * mm});
            skLineSegment(sketch, "E14.30.0.0", {"start": v(464.82, 31.75) * mm, "end": v(464.82, 35.71) * mm});
            skLineSegment(sketch, "E14.30.0.1", {"start": v(464.82, 35.71) * mm, "end": v(466.59, 41.46) * mm});
            skArc(sketch, "E14.30.0.2", {"start": v(467.2, 41.91) * mm, "mid": v(466.82, 41.79) * mm, "end": v(466.59, 41.46) * mm});
            skLineSegment(sketch, "E14.30.0.3", {"start": v(467.2, 41.91) * mm, "end": v(468.63, 41.91) * mm});
            skLineSegment(sketch, "E14.30.0.4", {"start": v(470.07, 41.91) * mm, "end": v(468.63, 41.91) * mm});
            skArc(sketch, "E14.30.0.5", {"start": v(470.67, 41.46) * mm, "mid": v(470.44, 41.79) * mm, "end": v(470.07, 41.91) * mm});
            skLineSegment(sketch, "E14.30.0.6", {"start": v(472.44, 35.71) * mm, "end": v(470.67, 41.46) * mm});
            skLineSegment(sketch, "E14.30.0.7", {"start": v(472.44, 35.71) * mm, "end": v(472.44, 31.75) * mm});
            skLineSegment(sketch, "E14.31.0.0", {"start": v(480.06, 31.75) * mm, "end": v(480.06, 35.71) * mm});
            skLineSegment(sketch, "E14.31.0.1", {"start": v(480.06, 35.71) * mm, "end": v(481.83, 41.46) * mm});
            skArc(sketch, "E14.31.0.2", {"start": v(482.43, 41.91) * mm, "mid": v(482.06, 41.79) * mm, "end": v(481.83, 41.46) * mm});
            skLineSegment(sketch, "E14.31.0.3", {"start": v(482.43, 41.91) * mm, "end": v(483.87, 41.91) * mm});
            skLineSegment(sketch, "E14.31.0.4", {"start": v(485.3, 41.91) * mm, "end": v(483.87, 41.91) * mm});
            skArc(sketch, "E14.31.0.5", {"start": v(485.91, 41.46) * mm, "mid": v(485.68, 41.79) * mm, "end": v(485.3, 41.91) * mm});
            skLineSegment(sketch, "E14.31.0.6", {"start": v(487.68, 35.71) * mm, "end": v(485.91, 41.46) * mm});
            skLineSegment(sketch, "E14.31.0.7", {"start": v(487.68, 35.71) * mm, "end": v(487.68, 31.75) * mm});
            skLineSegment(sketch, "E14.32.0.0", {"start": v(495.3, 31.75) * mm, "end": v(495.3, 35.71) * mm});
            skLineSegment(sketch, "E14.32.0.1", {"start": v(495.3, 35.71) * mm, "end": v(497.07, 41.46) * mm});
            skArc(sketch, "E14.32.0.2", {"start": v(497.67, 41.91) * mm, "mid": v(497.3, 41.79) * mm, "end": v(497.07, 41.46) * mm});
            skLineSegment(sketch, "E14.32.0.3", {"start": v(497.67, 41.91) * mm, "end": v(499.1, 41.91) * mm});
            skLineSegment(sketch, "E14.32.0.4", {"start": v(500.55, 41.91) * mm, "end": v(499.1, 41.91) * mm});
            skArc(sketch, "E14.32.0.5", {"start": v(501.15, 41.46) * mm, "mid": v(500.92, 41.79) * mm, "end": v(500.55, 41.91) * mm});
            skLineSegment(sketch, "E14.32.0.6", {"start": v(502.92, 35.71) * mm, "end": v(501.15, 41.46) * mm});
            skLineSegment(sketch, "E14.32.0.7", {"start": v(502.92, 35.71) * mm, "end": v(502.92, 31.75) * mm});
            skLineSegment(sketch, "E14.33.0.0", {"start": v(510.54, 31.75) * mm, "end": v(510.54, 35.71) * mm});
            skLineSegment(sketch, "E14.33.0.1", {"start": v(510.54, 35.71) * mm, "end": v(512.3, 41.46) * mm});
            skArc(sketch, "E14.33.0.2", {"start": v(512.91, 41.91) * mm, "mid": v(512.54, 41.79) * mm, "end": v(512.3, 41.46) * mm});
            skLineSegment(sketch, "E14.33.0.3", {"start": v(512.91, 41.91) * mm, "end": v(514.35, 41.91) * mm});
            skLineSegment(sketch, "E14.33.0.4", {"start": v(515.79, 41.91) * mm, "end": v(514.35, 41.91) * mm});
            skArc(sketch, "E14.33.0.5", {"start": v(516.4, 41.46) * mm, "mid": v(516.16, 41.79) * mm, "end": v(515.79, 41.91) * mm});
            skLineSegment(sketch, "E14.33.0.6", {"start": v(518.16, 35.71) * mm, "end": v(516.4, 41.46) * mm});
            skLineSegment(sketch, "E14.33.0.7", {"start": v(518.16, 35.71) * mm, "end": v(518.16, 31.75) * mm});
            skLineSegment(sketch, "E14.34.0.0", {"start": v(525.78, 31.75) * mm, "end": v(525.78, 35.71) * mm});
            skLineSegment(sketch, "E14.34.0.1", {"start": v(525.78, 35.71) * mm, "end": v(527.55, 41.46) * mm});
            skArc(sketch, "E14.34.0.2", {"start": v(528.15, 41.91) * mm, "mid": v(527.78, 41.79) * mm, "end": v(527.55, 41.46) * mm});
            skLineSegment(sketch, "E14.34.0.3", {"start": v(528.15, 41.91) * mm, "end": v(529.6, 41.91) * mm});
            skLineSegment(sketch, "E14.34.0.4", {"start": v(531.03, 41.91) * mm, "end": v(529.59, 41.91) * mm});
            skArc(sketch, "E14.34.0.5", {"start": v(531.63, 41.46) * mm, "mid": v(531.4, 41.79) * mm, "end": v(531.03, 41.91) * mm});
            skLineSegment(sketch, "E14.34.0.6", {"start": v(533.4, 35.71) * mm, "end": v(531.63, 41.46) * mm});
            skLineSegment(sketch, "E14.34.0.7", {"start": v(533.4, 35.71) * mm, "end": v(533.4, 31.75) * mm});
            skLineSegment(sketch, "E14.35.0.0", {"start": v(541.02, 31.75) * mm, "end": v(541.02, 35.71) * mm});
            skLineSegment(sketch, "E14.35.0.1", {"start": v(541.02, 35.71) * mm, "end": v(542.79, 41.46) * mm});
            skArc(sketch, "E14.35.0.2", {"start": v(543.4, 41.91) * mm, "mid": v(543.02, 41.79) * mm, "end": v(542.79, 41.46) * mm});
            skLineSegment(sketch, "E14.35.0.3", {"start": v(543.4, 41.91) * mm, "end": v(544.83, 41.91) * mm});
            skLineSegment(sketch, "E14.35.0.4", {"start": v(546.27, 41.91) * mm, "end": v(544.83, 41.91) * mm});
            skArc(sketch, "E14.35.0.5", {"start": v(546.87, 41.46) * mm, "mid": v(546.64, 41.79) * mm, "end": v(546.27, 41.91) * mm});
            skLineSegment(sketch, "E14.35.0.6", {"start": v(548.64, 35.71) * mm, "end": v(546.87, 41.46) * mm});
            skLineSegment(sketch, "E14.35.0.7", {"start": v(548.64, 35.71) * mm, "end": v(548.64, 31.75) * mm});
            skLineSegment(sketch, "E14.36.0.0", {"start": v(556.26, 31.75) * mm, "end": v(556.26, 35.71) * mm});
            skLineSegment(sketch, "E14.36.0.1", {"start": v(556.26, 35.71) * mm, "end": v(558.03, 41.46) * mm});
            skArc(sketch, "E14.36.0.2", {"start": v(558.63, 41.91) * mm, "mid": v(558.26, 41.79) * mm, "end": v(558.03, 41.46) * mm});
            skLineSegment(sketch, "E14.36.0.3", {"start": v(558.63, 41.91) * mm, "end": v(560.07, 41.91) * mm});
            skLineSegment(sketch, "E14.36.0.4", {"start": v(561.5, 41.91) * mm, "end": v(560.07, 41.91) * mm});
            skArc(sketch, "E14.36.0.5", {"start": v(562.11, 41.46) * mm, "mid": v(561.88, 41.79) * mm, "end": v(561.5, 41.91) * mm});
            skLineSegment(sketch, "E14.36.0.6", {"start": v(563.88, 35.71) * mm, "end": v(562.11, 41.46) * mm});
            skLineSegment(sketch, "E14.36.0.7", {"start": v(563.88, 35.71) * mm, "end": v(563.88, 31.75) * mm});
            skLineSegment(sketch, "E14.37.0.0", {"start": v(571.5, 31.75) * mm, "end": v(571.5, 35.71) * mm});
            skLineSegment(sketch, "E14.37.0.1", {"start": v(571.5, 35.71) * mm, "end": v(573.27, 41.46) * mm});
            skArc(sketch, "E14.37.0.2", {"start": v(573.87, 41.91) * mm, "mid": v(573.5, 41.79) * mm, "end": v(573.27, 41.46) * mm});
            skLineSegment(sketch, "E14.37.0.3", {"start": v(573.87, 41.91) * mm, "end": v(575.31, 41.91) * mm});
            skLineSegment(sketch, "E14.37.0.4", {"start": v(576.75, 41.91) * mm, "end": v(575.3, 41.91) * mm});
            skArc(sketch, "E14.37.0.5", {"start": v(577.35, 41.46) * mm, "mid": v(577.12, 41.79) * mm, "end": v(576.75, 41.91) * mm});
            skLineSegment(sketch, "E14.37.0.6", {"start": v(579.12, 35.71) * mm, "end": v(577.35, 41.46) * mm});
            skLineSegment(sketch, "E14.37.0.7", {"start": v(579.12, 35.71) * mm, "end": v(579.12, 31.75) * mm});
            skLineSegment(sketch, "E14.38.0.0", {"start": v(586.74, 31.75) * mm, "end": v(586.74, 35.71) * mm});
            skLineSegment(sketch, "E14.38.0.1", {"start": v(586.74, 35.71) * mm, "end": v(588.5, 41.46) * mm});
            skArc(sketch, "E14.38.0.2", {"start": v(589.11, 41.91) * mm, "mid": v(588.74, 41.79) * mm, "end": v(588.5, 41.46) * mm});
            skLineSegment(sketch, "E14.38.0.3", {"start": v(589.11, 41.91) * mm, "end": v(590.55, 41.91) * mm});
            skLineSegment(sketch, "E14.38.0.4", {"start": v(591.99, 41.91) * mm, "end": v(590.55, 41.91) * mm});
            skArc(sketch, "E14.38.0.5", {"start": v(592.6, 41.46) * mm, "mid": v(592.36, 41.79) * mm, "end": v(591.99, 41.91) * mm});
            skLineSegment(sketch, "E14.38.0.6", {"start": v(594.36, 35.71) * mm, "end": v(592.6, 41.46) * mm});
            skLineSegment(sketch, "E14.38.0.7", {"start": v(594.36, 35.71) * mm, "end": v(594.36, 31.75) * mm});
            skLineSegment(sketch, "E14.39.0.0", {"start": v(601.98, 31.75) * mm, "end": v(601.98, 35.71) * mm});
            skLineSegment(sketch, "E14.39.0.1", {"start": v(601.98, 35.71) * mm, "end": v(603.75, 41.46) * mm});
            skArc(sketch, "E14.39.0.2", {"start": v(604.35, 41.91) * mm, "mid": v(603.98, 41.79) * mm, "end": v(603.75, 41.46) * mm});
            skLineSegment(sketch, "E14.39.0.3", {"start": v(604.35, 41.91) * mm, "end": v(605.8, 41.91) * mm});
            skLineSegment(sketch, "E14.39.0.4", {"start": v(607.23, 41.91) * mm, "end": v(605.8, 41.91) * mm});
            skArc(sketch, "E14.39.0.5", {"start": v(607.83, 41.46) * mm, "mid": v(607.6, 41.79) * mm, "end": v(607.23, 41.91) * mm});
            skLineSegment(sketch, "E14.39.0.6", {"start": v(609.6, 35.71) * mm, "end": v(607.83, 41.46) * mm});
            skLineSegment(sketch, "E14.39.0.7", {"start": v(609.6, 35.71) * mm, "end": v(609.6, 31.75) * mm});
            skLineSegment(sketch, "E14.40.0.0", {"start": v(617.22, 31.75) * mm, "end": v(617.22, 35.71) * mm});
            skLineSegment(sketch, "E14.40.0.1", {"start": v(617.22, 35.71) * mm, "end": v(618.99, 41.46) * mm});
            skArc(sketch, "E14.40.0.2", {"start": v(619.6, 41.91) * mm, "mid": v(619.22, 41.79) * mm, "end": v(618.99, 41.46) * mm});
            skLineSegment(sketch, "E14.40.0.3", {"start": v(619.6, 41.91) * mm, "end": v(621.03, 41.91) * mm});
            skLineSegment(sketch, "E14.40.0.4", {"start": v(622.47, 41.91) * mm, "end": v(621.03, 41.91) * mm});
            skArc(sketch, "E14.40.0.5", {"start": v(623.07, 41.46) * mm, "mid": v(622.84, 41.79) * mm, "end": v(622.47, 41.91) * mm});
            skLineSegment(sketch, "E14.40.0.6", {"start": v(624.84, 35.71) * mm, "end": v(623.07, 41.46) * mm});
            skLineSegment(sketch, "E14.40.0.7", {"start": v(624.84, 35.71) * mm, "end": v(624.84, 31.75) * mm});
            skLineSegment(sketch, "E14.41.0.0", {"start": v(632.46, 31.75) * mm, "end": v(632.46, 35.71) * mm});
            skLineSegment(sketch, "E14.41.0.1", {"start": v(632.46, 35.71) * mm, "end": v(634.23, 41.46) * mm});
            skArc(sketch, "E14.41.0.2", {"start": v(634.83, 41.91) * mm, "mid": v(634.46, 41.79) * mm, "end": v(634.23, 41.46) * mm});
            skLineSegment(sketch, "E14.41.0.3", {"start": v(634.83, 41.91) * mm, "end": v(636.27, 41.91) * mm});
            skLineSegment(sketch, "E14.41.0.4", {"start": v(637.7, 41.91) * mm, "end": v(636.27, 41.91) * mm});
            skArc(sketch, "E14.41.0.5", {"start": v(638.31, 41.46) * mm, "mid": v(638.08, 41.79) * mm, "end": v(637.7, 41.91) * mm});
            skLineSegment(sketch, "E14.41.0.6", {"start": v(640.08, 35.71) * mm, "end": v(638.31, 41.46) * mm});
            skLineSegment(sketch, "E14.41.0.7", {"start": v(640.08, 35.71) * mm, "end": v(640.08, 31.75) * mm});
            skLineSegment(sketch, "E14.42.0.0", {"start": v(647.7, 31.75) * mm, "end": v(647.7, 35.71) * mm});
            skLineSegment(sketch, "E14.42.0.1", {"start": v(647.7, 35.71) * mm, "end": v(649.47, 41.46) * mm});
            skArc(sketch, "E14.42.0.2", {"start": v(650.07, 41.91) * mm, "mid": v(649.7, 41.79) * mm, "end": v(649.47, 41.46) * mm});
            skLineSegment(sketch, "E14.42.0.3", {"start": v(650.07, 41.91) * mm, "end": v(651.5, 41.91) * mm});
            skLineSegment(sketch, "E14.42.0.4", {"start": v(652.95, 41.91) * mm, "end": v(651.5, 41.91) * mm});
            skArc(sketch, "E14.42.0.5", {"start": v(653.55, 41.46) * mm, "mid": v(653.32, 41.79) * mm, "end": v(652.95, 41.91) * mm});
            skLineSegment(sketch, "E14.42.0.6", {"start": v(655.32, 35.71) * mm, "end": v(653.55, 41.46) * mm});
            skLineSegment(sketch, "E14.42.0.7", {"start": v(655.32, 35.71) * mm, "end": v(655.32, 31.75) * mm});
            skLineSegment(sketch, "E14.43.0.0", {"start": v(662.94, 31.75) * mm, "end": v(662.94, 35.71) * mm});
            skLineSegment(sketch, "E14.43.0.1", {"start": v(662.94, 35.71) * mm, "end": v(664.7, 41.46) * mm});
            skArc(sketch, "E14.43.0.2", {"start": v(665.31, 41.91) * mm, "mid": v(664.94, 41.79) * mm, "end": v(664.7, 41.46) * mm});
            skLineSegment(sketch, "E14.43.0.3", {"start": v(665.31, 41.91) * mm, "end": v(666.75, 41.91) * mm});
            skLineSegment(sketch, "E14.43.0.4", {"start": v(668.19, 41.91) * mm, "end": v(666.75, 41.91) * mm});
            skArc(sketch, "E14.43.0.5", {"start": v(668.8, 41.46) * mm, "mid": v(668.56, 41.79) * mm, "end": v(668.19, 41.91) * mm});
            skLineSegment(sketch, "E14.43.0.6", {"start": v(670.56, 35.71) * mm, "end": v(668.8, 41.46) * mm});
            skLineSegment(sketch, "E14.43.0.7", {"start": v(670.56, 35.71) * mm, "end": v(670.56, 31.75) * mm});
            skLineSegment(sketch, "E14.44.0.0", {"start": v(678.18, 31.75) * mm, "end": v(678.18, 35.71) * mm});
            skLineSegment(sketch, "E14.44.0.1", {"start": v(678.18, 35.71) * mm, "end": v(679.95, 41.46) * mm});
            skArc(sketch, "E14.44.0.2", {"start": v(680.55, 41.91) * mm, "mid": v(680.18, 41.79) * mm, "end": v(679.95, 41.46) * mm});
            skLineSegment(sketch, "E14.44.0.3", {"start": v(680.55, 41.91) * mm, "end": v(682, 41.91) * mm});
            skLineSegment(sketch, "E14.44.0.4", {"start": v(683.43, 41.91) * mm, "end": v(682, 41.91) * mm});
            skArc(sketch, "E14.44.0.5", {"start": v(684.03, 41.46) * mm, "mid": v(683.8, 41.79) * mm, "end": v(683.43, 41.91) * mm});
            skLineSegment(sketch, "E14.44.0.6", {"start": v(685.8, 35.71) * mm, "end": v(684.03, 41.46) * mm});
            skLineSegment(sketch, "E14.44.0.7", {"start": v(685.8, 35.71) * mm, "end": v(685.8, 31.75) * mm});
            skLineSegment(sketch, "E14.45.0.0", {"start": v(693.42, 31.75) * mm, "end": v(693.42, 35.71) * mm});
            skLineSegment(sketch, "E14.45.0.1", {"start": v(693.42, 35.71) * mm, "end": v(695.19, 41.46) * mm});
            skArc(sketch, "E14.45.0.2", {"start": v(695.8, 41.91) * mm, "mid": v(695.42, 41.79) * mm, "end": v(695.19, 41.46) * mm});
            skLineSegment(sketch, "E14.45.0.3", {"start": v(695.8, 41.91) * mm, "end": v(697.23, 41.91) * mm});
            skLineSegment(sketch, "E14.45.0.4", {"start": v(698.67, 41.91) * mm, "end": v(697.23, 41.91) * mm});
            skArc(sketch, "E14.45.0.5", {"start": v(699.27, 41.46) * mm, "mid": v(699.04, 41.79) * mm, "end": v(698.67, 41.91) * mm});
            skLineSegment(sketch, "E14.45.0.6", {"start": v(701.04, 35.71) * mm, "end": v(699.27, 41.46) * mm});
            skLineSegment(sketch, "E14.45.0.7", {"start": v(701.04, 35.71) * mm, "end": v(701.04, 31.75) * mm});
            skLineSegment(sketch, "E14.46.0.0", {"start": v(708.66, 31.75) * mm, "end": v(708.66, 35.71) * mm});
            skLineSegment(sketch, "E14.46.0.1", {"start": v(708.66, 35.71) * mm, "end": v(710.43, 41.46) * mm});
            skArc(sketch, "E14.46.0.2", {"start": v(711.03, 41.91) * mm, "mid": v(710.66, 41.79) * mm, "end": v(710.43, 41.46) * mm});
            skLineSegment(sketch, "E14.46.0.3", {"start": v(711.03, 41.91) * mm, "end": v(712.47, 41.91) * mm});
            skLineSegment(sketch, "E14.46.0.4", {"start": v(713.9, 41.91) * mm, "end": v(712.47, 41.91) * mm});
            skArc(sketch, "E14.46.0.5", {"start": v(714.51, 41.46) * mm, "mid": v(714.28, 41.79) * mm, "end": v(713.9, 41.91) * mm});
            skLineSegment(sketch, "E14.46.0.6", {"start": v(716.28, 35.71) * mm, "end": v(714.51, 41.46) * mm});
            skLineSegment(sketch, "E14.46.0.7", {"start": v(716.28, 35.71) * mm, "end": v(716.28, 31.75) * mm});
            skLineSegment(sketch, "E14.47.0.0", {"start": v(723.9, 31.75) * mm, "end": v(723.9, 35.71) * mm});
            skLineSegment(sketch, "E14.47.0.1", {"start": v(723.9, 35.71) * mm, "end": v(725.67, 41.46) * mm});
            skArc(sketch, "E14.47.0.2", {"start": v(726.27, 41.91) * mm, "mid": v(725.9, 41.79) * mm, "end": v(725.67, 41.46) * mm});
            skLineSegment(sketch, "E14.47.0.3", {"start": v(726.27, 41.91) * mm, "end": v(727.7, 41.91) * mm});
            skLineSegment(sketch, "E14.47.0.4", {"start": v(729.15, 41.91) * mm, "end": v(727.7, 41.91) * mm});
            skArc(sketch, "E14.47.0.5", {"start": v(729.75, 41.46) * mm, "mid": v(729.52, 41.79) * mm, "end": v(729.15, 41.91) * mm});
            skLineSegment(sketch, "E14.47.0.6", {"start": v(731.52, 35.71) * mm, "end": v(729.75, 41.46) * mm});
            skLineSegment(sketch, "E14.47.0.7", {"start": v(731.52, 35.71) * mm, "end": v(731.52, 31.75) * mm});
            skLineSegment(sketch, "E14.48.0.0", {"start": v(739.14, 31.75) * mm, "end": v(739.14, 35.71) * mm});
            skLineSegment(sketch, "E14.48.0.1", {"start": v(739.14, 35.71) * mm, "end": v(740.9, 41.46) * mm});
            skArc(sketch, "E14.48.0.2", {"start": v(741.51, 41.91) * mm, "mid": v(741.14, 41.79) * mm, "end": v(740.9, 41.46) * mm});
            skLineSegment(sketch, "E14.48.0.3", {"start": v(741.51, 41.91) * mm, "end": v(742.95, 41.91) * mm});
            skLineSegment(sketch, "E14.48.0.4", {"start": v(744.39, 41.91) * mm, "end": v(742.95, 41.91) * mm});
            skArc(sketch, "E14.48.0.5", {"start": v(745, 41.46) * mm, "mid": v(744.76, 41.79) * mm, "end": v(744.39, 41.91) * mm});
            skLineSegment(sketch, "E14.48.0.6", {"start": v(746.76, 35.71) * mm, "end": v(745, 41.46) * mm});
            skLineSegment(sketch, "E14.48.0.7", {"start": v(746.76, 35.71) * mm, "end": v(746.76, 31.75) * mm});
            skLineSegment(sketch, "E14.49.0.0", {"start": v(754.38, 31.75) * mm, "end": v(754.38, 35.71) * mm});
            skLineSegment(sketch, "E14.49.0.1", {"start": v(754.38, 35.71) * mm, "end": v(756.15, 41.46) * mm});
            skArc(sketch, "E14.49.0.2", {"start": v(756.75, 41.91) * mm, "mid": v(756.38, 41.79) * mm, "end": v(756.15, 41.46) * mm});
            skLineSegment(sketch, "E14.49.0.3", {"start": v(756.75, 41.91) * mm, "end": v(758.2, 41.91) * mm});
            skLineSegment(sketch, "E14.49.0.4", {"start": v(759.63, 41.91) * mm, "end": v(758.19, 41.91) * mm});
            skArc(sketch, "E14.49.0.5", {"start": v(760.23, 41.46) * mm, "mid": v(760, 41.79) * mm, "end": v(759.63, 41.91) * mm});
            skLineSegment(sketch, "E14.49.0.6", {"start": v(762, 35.71) * mm, "end": v(760.23, 41.46) * mm});
            skLineSegment(sketch, "E14.49.0.7", {"start": v(762, 35.71) * mm, "end": v(762, 31.75) * mm});
            skLineSegment(sketch, "E14.direction1", {"start": v(7.62, 31.75) * mm, "end": v(22.86, 31.75) * mm, "construction": true});
            skSolve(sketch);
        }
        {
            var Q0;
            Q0 = qSketchRegion(id + "F0", true);
            extrude(context, id + "F1", {"entities" : qUnion([Q0]), "depth" : 152.4 * mm});
        }
        {
            var Q0;
            Q0=makeQuery(id+"F1.opExtrude","CAP_FACE",FACE,{"disambiguationData":[OSD([sQuery(id+"F0.wireOp",EDGE,"E0.bottom"),sQuery(id+"F0.wireOp",EDGE,"E0.top"),sQuery(id+"F0.wireOp",EDGE,"E0.left"),sQuery(id+"F0.wireOp",EDGE,"E0.right"),sQuery(id+"F0.wireOp",EDGE,"E4"),sQuery(id+"F0.wireOp",EDGE,"E6"),sQuery(id+"F0.wireOp",EDGE,"E7"),sQuery(id+"F0.wireOp",EDGE,"E8"),sQuery(id+"F0.wireOp",EDGE,"E9"),sQuery(id+"F0.wireOp",EDGE,"E10"),sQuery(id+"F0.wireOp",EDGE,"E12.filletArc"),sQuery(id+"F0.wireOp",EDGE,"E13.filletArc"),sQuery(id+"F0.wireOp",EDGE,"E14.1.0.0"),sQuery(id+"F0.wireOp",EDGE,"E14.1.0.1"),sQuery(id+"F0.wireOp",EDGE,"E14.1.0.2"),sQuery(id+"F0.wireOp",EDGE,"E14.1.0.3"),sQuery(id+"F0.wireOp",EDGE,"E14.1.0.4"),sQuery(id+"F0.wireOp",EDGE,"E14.1.0.5"),sQuery(id+"F0.wireOp",EDGE,"E14.1.0.6"),sQuery(id+"F0.wireOp",EDGE,"E14.1.0.7"),sQuery(id+"F0.wireOp",EDGE,"E14.2.0.0"),sQuery(id+"F0.wireOp",EDGE,"E14.2.0.1"),sQuery(id+"F0.wireOp",EDGE,"E14.2.0.2"),sQuery(id+"F0.wireOp",EDGE,"E14.2.0.3"),sQuery(id+"F0.wireOp",EDGE,"E14.2.0.4"),sQuery(id+"F0.wireOp",EDGE,"E14.2.0.5"),sQuery(id+"F0.wireOp",EDGE,"E14.2.0.6"),sQuery(id+"F0.wireOp",EDGE,"E14.2.0.7"),sQuery(id+"F0.wireOp",EDGE,"E14.3.0.0"),sQuery(id+"F0.wireOp",EDGE,"E14.3.0.1"),sQuery(id+"F0.wireOp",EDGE,"E14.3.0.2"),sQuery(id+"F0.wireOp",EDGE,"E14.3.0.3"),sQuery(id+"F0.wireOp",EDGE,"E14.3.0.4"),sQuery(id+"F0.wireOp",EDGE,"E14.3.0.5"),sQuery(id+"F0.wireOp",EDGE,"E14.3.0.6"),sQuery(id+"F0.wireOp",EDGE,"E14.3.0.7"),sQuery(id+"F0.wireOp",EDGE,"E14.4.0.0"),sQuery(id+"F0.wireOp",EDGE,"E14.4.0.1"),sQuery(id+"F0.wireOp",EDGE,"E14.4.0.2"),sQuery(id+"F0.wireOp",EDGE,"E14.4.0.3"),sQuery(id+"F0.wireOp",EDGE,"E14.4.0.4"),sQuery(id+"F0.wireOp",EDGE,"E14.4.0.5"),sQuery(id+"F0.wireOp",EDGE,"E14.4.0.6"),sQuery(id+"F0.wireOp",EDGE,"E14.4.0.7"),sQuery(id+"F0.wireOp",EDGE,"E14.5.0.0"),sQuery(id+"F0.wireOp",EDGE,"E14.5.0.1"),sQuery(id+"F0.wireOp",EDGE,"E14.5.0.2"),sQuery(id+"F0.wireOp",EDGE,"E14.5.0.3"),sQuery(id+"F0.wireOp",EDGE,"E14.5.0.4"),sQuery(id+"F0.wireOp",EDGE,"E14.5.0.5"),sQuery(id+"F0.wireOp",EDGE,"E14.5.0.6"),sQuery(id+"F0.wireOp",EDGE,"E14.5.0.7"),sQuery(id+"F0.wireOp",EDGE,"E14.6.0.0"),sQuery(id+"F0.wireOp",EDGE,"E14.6.0.1"),sQuery(id+"F0.wireOp",EDGE,"E14.6.0.2"),sQuery(id+"F0.wireOp",EDGE,"E14.6.0.3"),sQuery(id+"F0.wireOp",EDGE,"E14.6.0.4"),sQuery(id+"F0.wireOp",EDGE,"E14.6.0.5"),sQuery(id+"F0.wireOp",EDGE,"E14.6.0.6"),sQuery(id+"F0.wireOp",EDGE,"E14.6.0.7"),sQuery(id+"F0.wireOp",EDGE,"E14.7.0.0"),sQuery(id+"F0.wireOp",EDGE,"E14.7.0.1"),sQuery(id+"F0.wireOp",EDGE,"E14.7.0.2"),sQuery(id+"F0.wireOp",EDGE,"E14.7.0.3"),sQuery(id+"F0.wireOp",EDGE,"E14.7.0.4"),sQuery(id+"F0.wireOp",EDGE,"E14.7.0.5"),sQuery(id+"F0.wireOp",EDGE,"E14.7.0.6"),sQuery(id+"F0.wireOp",EDGE,"E14.7.0.7"),sQuery(id+"F0.wireOp",EDGE,"E14.8.0.0"),sQuery(id+"F0.wireOp",EDGE,"E14.8.0.1"),sQuery(id+"F0.wireOp",EDGE,"E14.8.0.2"),sQuery(id+"F0.wireOp",EDGE,"E14.8.0.3"),sQuery(id+"F0.wireOp",EDGE,"E14.8.0.4"),sQuery(id+"F0.wireOp",EDGE,"E14.8.0.5"),sQuery(id+"F0.wireOp",EDGE,"E14.8.0.6"),sQuery(id+"F0.wireOp",EDGE,"E14.8.0.7"),sQuery(id+"F0.wireOp",EDGE,"E14.9.0.0"),sQuery(id+"F0.wireOp",EDGE,"E14.9.0.1"),sQuery(id+"F0.wireOp",EDGE,"E14.9.0.2"),sQuery(id+"F0.wireOp",EDGE,"E14.9.0.3"),sQuery(id+"F0.wireOp",EDGE,"E14.9.0.4"),sQuery(id+"F0.wireOp",EDGE,"E14.9.0.5"),sQuery(id+"F0.wireOp",EDGE,"E14.9.0.6"),sQuery(id+"F0.wireOp",EDGE,"E14.9.0.7"),sQuery(id+"F0.wireOp",EDGE,"E14.10.0.0"),sQuery(id+"F0.wireOp",EDGE,"E14.10.0.1"),sQuery(id+"F0.wireOp",EDGE,"E14.10.0.2"),sQuery(id+"F0.wireOp",EDGE,"E14.10.0.3"),sQuery(id+"F0.wireOp",EDGE,"E14.10.0.4"),sQuery(id+"F0.wireOp",EDGE,"E14.10.0.5"),sQuery(id+"F0.wireOp",EDGE,"E14.10.0.6"),sQuery(id+"F0.wireOp",EDGE,"E14.10.0.7"),sQuery(id+"F0.wireOp",EDGE,"E14.11.0.0"),sQuery(id+"F0.wireOp",EDGE,"E14.11.0.1"),sQuery(id+"F0.wireOp",EDGE,"E14.11.0.2"),sQuery(id+"F0.wireOp",EDGE,"E14.11.0.3"),sQuery(id+"F0.wireOp",EDGE,"E14.11.0.4"),sQuery(id+"F0.wireOp",EDGE,"E14.11.0.5"),sQuery(id+"F0.wireOp",EDGE,"E14.11.0.6"),sQuery(id+"F0.wireOp",EDGE,"E14.11.0.7"),sQuery(id+"F0.wireOp",EDGE,"E14.12.0.0"),sQuery(id+"F0.wireOp",EDGE,"E14.12.0.1"),sQuery(id+"F0.wireOp",EDGE,"E14.12.0.2"),sQuery(id+"F0.wireOp",EDGE,"E14.12.0.3"),sQuery(id+"F0.wireOp",EDGE,"E14.12.0.4"),sQuery(id+"F0.wireOp",EDGE,"E14.12.0.5"),sQuery(id+"F0.wireOp",EDGE,"E14.12.0.6"),sQuery(id+"F0.wireOp",EDGE,"E14.12.0.7"),sQuery(id+"F0.wireOp",EDGE,"E14.13.0.0"),sQuery(id+"F0.wireOp",EDGE,"E14.13.0.1"),sQuery(id+"F0.wireOp",EDGE,"E14.13.0.2"),sQuery(id+"F0.wireOp",EDGE,"E14.13.0.3"),sQuery(id+"F0.wireOp",EDGE,"E14.13.0.4"),sQuery(id+"F0.wireOp",EDGE,"E14.13.0.5"),sQuery(id+"F0.wireOp",EDGE,"E14.13.0.6"),sQuery(id+"F0.wireOp",EDGE,"E14.13.0.7"),sQuery(id+"F0.wireOp",EDGE,"E14.14.0.0"),sQuery(id+"F0.wireOp",EDGE,"E14.14.0.1"),sQuery(id+"F0.wireOp",EDGE,"E14.14.0.2"),sQuery(id+"F0.wireOp",EDGE,"E14.14.0.3"),sQuery(id+"F0.wireOp",EDGE,"E14.14.0.4"),sQuery(id+"F0.wireOp",EDGE,"E14.14.0.5"),sQuery(id+"F0.wireOp",EDGE,"E14.14.0.6"),sQuery(id+"F0.wireOp",EDGE,"E14.14.0.7"),sQuery(id+"F0.wireOp",EDGE,"E14.15.0.0"),sQuery(id+"F0.wireOp",EDGE,"E14.15.0.1"),sQuery(id+"F0.wireOp",EDGE,"E14.15.0.2"),sQuery(id+"F0.wireOp",EDGE,"E14.15.0.3"),sQuery(id+"F0.wireOp",EDGE,"E14.15.0.4"),sQuery(id+"F0.wireOp",EDGE,"E14.15.0.5"),sQuery(id+"F0.wireOp",EDGE,"E14.15.0.6"),sQuery(id+"F0.wireOp",EDGE,"E14.15.0.7"),sQuery(id+"F0.wireOp",EDGE,"E14.16.0.0"),sQuery(id+"F0.wireOp",EDGE,"E14.16.0.1"),sQuery(id+"F0.wireOp",EDGE,"E14.16.0.2"),sQuery(id+"F0.wireOp",EDGE,"E14.16.0.3"),sQuery(id+"F0.wireOp",EDGE,"E14.16.0.4"),sQuery(id+"F0.wireOp",EDGE,"E14.16.0.5"),sQuery(id+"F0.wireOp",EDGE,"E14.16.0.6"),sQuery(id+"F0.wireOp",EDGE,"E14.16.0.7"),sQuery(id+"F0.wireOp",EDGE,"E14.17.0.0"),sQuery(id+"F0.wireOp",EDGE,"E14.17.0.1"),sQuery(id+"F0.wireOp",EDGE,"E14.17.0.2"),sQuery(id+"F0.wireOp",EDGE,"E14.17.0.3"),sQuery(id+"F0.wireOp",EDGE,"E14.17.0.4"),sQuery(id+"F0.wireOp",EDGE,"E14.17.0.5"),sQuery(id+"F0.wireOp",EDGE,"E14.17.0.6"),sQuery(id+"F0.wireOp",EDGE,"E14.17.0.7"),sQuery(id+"F0.wireOp",EDGE,"E14.18.0.0"),sQuery(id+"F0.wireOp",EDGE,"E14.18.0.1"),sQuery(id+"F0.wireOp",EDGE,"E14.18.0.2"),sQuery(id+"F0.wireOp",EDGE,"E14.18.0.3"),sQuery(id+"F0.wireOp",EDGE,"E14.18.0.4"),sQuery(id+"F0.wireOp",EDGE,"E14.18.0.5"),sQuery(id+"F0.wireOp",EDGE,"E14.18.0.6"),sQuery(id+"F0.wireOp",EDGE,"E14.18.0.7"),sQuery(id+"F0.wireOp",EDGE,"E14.19.0.0"),sQuery(id+"F0.wireOp",EDGE,"E14.19.0.1"),sQuery(id+"F0.wireOp",EDGE,"E14.19.0.2"),sQuery(id+"F0.wireOp",EDGE,"E14.19.0.3"),sQuery(id+"F0.wireOp",EDGE,"E14.19.0.4"),sQuery(id+"F0.wireOp",EDGE,"E14.19.0.5"),sQuery(id+"F0.wireOp",EDGE,"E14.19.0.6"),sQuery(id+"F0.wireOp",EDGE,"E14.19.0.7"),sQuery(id+"F0.wireOp",EDGE,"E14.20.0.0"),sQuery(id+"F0.wireOp",EDGE,"E14.20.0.1"),sQuery(id+"F0.wireOp",EDGE,"E14.20.0.2"),sQuery(id+"F0.wireOp",EDGE,"E14.20.0.3"),sQuery(id+"F0.wireOp",EDGE,"E14.20.0.4"),sQuery(id+"F0.wireOp",EDGE,"E14.20.0.5"),sQuery(id+"F0.wireOp",EDGE,"E14.20.0.6"),sQuery(id+"F0.wireOp",EDGE,"E14.20.0.7"),sQuery(id+"F0.wireOp",EDGE,"E14.21.0.0"),sQuery(id+"F0.wireOp",EDGE,"E14.21.0.1"),sQuery(id+"F0.wireOp",EDGE,"E14.21.0.2"),sQuery(id+"F0.wireOp",EDGE,"E14.21.0.3"),sQuery(id+"F0.wireOp",EDGE,"E14.21.0.4"),sQuery(id+"F0.wireOp",EDGE,"E14.21.0.5"),sQuery(id+"F0.wireOp",EDGE,"E14.21.0.6"),sQuery(id+"F0.wireOp",EDGE,"E14.21.0.7"),sQuery(id+"F0.wireOp",EDGE,"E14.22.0.0"),sQuery(id+"F0.wireOp",EDGE,"E14.22.0.1"),sQuery(id+"F0.wireOp",EDGE,"E14.22.0.2"),sQuery(id+"F0.wireOp",EDGE,"E14.22.0.3"),sQuery(id+"F0.wireOp",EDGE,"E14.22.0.4"),sQuery(id+"F0.wireOp",EDGE,"E14.22.0.5"),sQuery(id+"F0.wireOp",EDGE,"E14.22.0.6"),sQuery(id+"F0.wireOp",EDGE,"E14.22.0.7"),sQuery(id+"F0.wireOp",EDGE,"E14.23.0.0"),sQuery(id+"F0.wireOp",EDGE,"E14.23.0.1"),sQuery(id+"F0.wireOp",EDGE,"E14.23.0.2"),sQuery(id+"F0.wireOp",EDGE,"E14.23.0.3"),sQuery(id+"F0.wireOp",EDGE,"E14.23.0.4"),sQuery(id+"F0.wireOp",EDGE,"E14.23.0.5"),sQuery(id+"F0.wireOp",EDGE,"E14.23.0.6"),sQuery(id+"F0.wireOp",EDGE,"E14.23.0.7"),sQuery(id+"F0.wireOp",EDGE,"E14.24.0.0"),sQuery(id+"F0.wireOp",EDGE,"E14.24.0.1"),sQuery(id+"F0.wireOp",EDGE,"E14.24.0.2"),sQuery(id+"F0.wireOp",EDGE,"E14.24.0.3"),sQuery(id+"F0.wireOp",EDGE,"E14.24.0.4"),sQuery(id+"F0.wireOp",EDGE,"E14.24.0.5"),sQuery(id+"F0.wireOp",EDGE,"E14.24.0.6"),sQuery(id+"F0.wireOp",EDGE,"E14.24.0.7"),sQuery(id+"F0.wireOp",EDGE,"E14.25.0.0"),sQuery(id+"F0.wireOp",EDGE,"E14.25.0.1"),sQuery(id+"F0.wireOp",EDGE,"E14.25.0.2"),sQuery(id+"F0.wireOp",EDGE,"E14.25.0.3"),sQuery(id+"F0.wireOp",EDGE,"E14.25.0.4"),sQuery(id+"F0.wireOp",EDGE,"E14.25.0.5"),sQuery(id+"F0.wireOp",EDGE,"E14.25.0.6"),sQuery(id+"F0.wireOp",EDGE,"E14.25.0.7"),sQuery(id+"F0.wireOp",EDGE,"E14.26.0.0"),sQuery(id+"F0.wireOp",EDGE,"E14.26.0.1"),sQuery(id+"F0.wireOp",EDGE,"E14.26.0.2"),sQuery(id+"F0.wireOp",EDGE,"E14.26.0.3"),sQuery(id+"F0.wireOp",EDGE,"E14.26.0.4"),sQuery(id+"F0.wireOp",EDGE,"E14.26.0.5"),sQuery(id+"F0.wireOp",EDGE,"E14.26.0.6"),sQuery(id+"F0.wireOp",EDGE,"E14.26.0.7"),sQuery(id+"F0.wireOp",EDGE,"E14.27.0.0"),sQuery(id+"F0.wireOp",EDGE,"E14.27.0.1"),sQuery(id+"F0.wireOp",EDGE,"E14.27.0.2"),sQuery(id+"F0.wireOp",EDGE,"E14.27.0.3"),sQuery(id+"F0.wireOp",EDGE,"E14.27.0.4"),sQuery(id+"F0.wireOp",EDGE,"E14.27.0.5"),sQuery(id+"F0.wireOp",EDGE,"E14.27.0.6"),sQuery(id+"F0.wireOp",EDGE,"E14.27.0.7"),sQuery(id+"F0.wireOp",EDGE,"E14.28.0.0"),sQuery(id+"F0.wireOp",EDGE,"E14.28.0.1"),sQuery(id+"F0.wireOp",EDGE,"E14.28.0.2"),sQuery(id+"F0.wireOp",EDGE,"E14.28.0.3"),sQuery(id+"F0.wireOp",EDGE,"E14.28.0.4"),sQuery(id+"F0.wireOp",EDGE,"E14.28.0.5"),sQuery(id+"F0.wireOp",EDGE,"E14.28.0.6"),sQuery(id+"F0.wireOp",EDGE,"E14.28.0.7"),sQuery(id+"F0.wireOp",EDGE,"E14.29.0.0"),sQuery(id+"F0.wireOp",EDGE,"E14.29.0.1"),sQuery(id+"F0.wireOp",EDGE,"E14.29.0.2"),sQuery(id+"F0.wireOp",EDGE,"E14.29.0.3"),sQuery(id+"F0.wireOp",EDGE,"E14.29.0.4"),sQuery(id+"F0.wireOp",EDGE,"E14.29.0.5"),sQuery(id+"F0.wireOp",EDGE,"E14.29.0.6"),sQuery(id+"F0.wireOp",EDGE,"E14.29.0.7"),sQuery(id+"F0.wireOp",EDGE,"E14.30.0.0"),sQuery(id+"F0.wireOp",EDGE,"E14.30.0.1"),sQuery(id+"F0.wireOp",EDGE,"E14.30.0.2"),sQuery(id+"F0.wireOp",EDGE,"E14.30.0.3"),sQuery(id+"F0.wireOp",EDGE,"E14.30.0.4"),sQuery(id+"F0.wireOp",EDGE,"E14.30.0.5"),sQuery(id+"F0.wireOp",EDGE,"E14.30.0.6"),sQuery(id+"F0.wireOp",EDGE,"E14.30.0.7"),sQuery(id+"F0.wireOp",EDGE,"E14.31.0.0"),sQuery(id+"F0.wireOp",EDGE,"E14.31.0.1"),sQuery(id+"F0.wireOp",EDGE,"E14.31.0.2"),sQuery(id+"F0.wireOp",EDGE,"E14.31.0.3"),sQuery(id+"F0.wireOp",EDGE,"E14.31.0.4"),sQuery(id+"F0.wireOp",EDGE,"E14.31.0.5"),sQuery(id+"F0.wireOp",EDGE,"E14.31.0.6"),sQuery(id+"F0.wireOp",EDGE,"E14.31.0.7"),sQuery(id+"F0.wireOp",EDGE,"E14.32.0.0"),sQuery(id+"F0.wireOp",EDGE,"E14.32.0.1"),sQuery(id+"F0.wireOp",EDGE,"E14.32.0.2"),sQuery(id+"F0.wireOp",EDGE,"E14.32.0.3"),sQuery(id+"F0.wireOp",EDGE,"E14.32.0.4"),sQuery(id+"F0.wireOp",EDGE,"E14.32.0.5"),sQuery(id+"F0.wireOp",EDGE,"E14.32.0.6"),sQuery(id+"F0.wireOp",EDGE,"E14.32.0.7"),sQuery(id+"F0.wireOp",EDGE,"E14.33.0.0"),sQuery(id+"F0.wireOp",EDGE,"E14.33.0.1"),sQuery(id+"F0.wireOp",EDGE,"E14.33.0.2"),sQuery(id+"F0.wireOp",EDGE,"E14.33.0.3"),sQuery(id+"F0.wireOp",EDGE,"E14.33.0.4"),sQuery(id+"F0.wireOp",EDGE,"E14.33.0.5"),sQuery(id+"F0.wireOp",EDGE,"E14.33.0.6"),sQuery(id+"F0.wireOp",EDGE,"E14.33.0.7"),sQuery(id+"F0.wireOp",EDGE,"E14.34.0.0"),sQuery(id+"F0.wireOp",EDGE,"E14.34.0.1"),sQuery(id+"F0.wireOp",EDGE,"E14.34.0.2"),sQuery(id+"F0.wireOp",EDGE,"E14.34.0.3"),sQuery(id+"F0.wireOp",EDGE,"E14.34.0.4"),sQuery(id+"F0.wireOp",EDGE,"E14.34.0.5"),sQuery(id+"F0.wireOp",EDGE,"E14.34.0.6"),sQuery(id+"F0.wireOp",EDGE,"E14.34.0.7"),sQuery(id+"F0.wireOp",EDGE,"E14.35.0.0"),sQuery(id+"F0.wireOp",EDGE,"E14.35.0.1"),sQuery(id+"F0.wireOp",EDGE,"E14.35.0.2"),sQuery(id+"F0.wireOp",EDGE,"E14.35.0.3"),sQuery(id+"F0.wireOp",EDGE,"E14.35.0.4"),sQuery(id+"F0.wireOp",EDGE,"E14.35.0.5"),sQuery(id+"F0.wireOp",EDGE,"E14.35.0.6"),sQuery(id+"F0.wireOp",EDGE,"E14.35.0.7"),sQuery(id+"F0.wireOp",EDGE,"E14.36.0.0"),sQuery(id+"F0.wireOp",EDGE,"E14.36.0.1"),sQuery(id+"F0.wireOp",EDGE,"E14.36.0.2"),sQuery(id+"F0.wireOp",EDGE,"E14.36.0.3"),sQuery(id+"F0.wireOp",EDGE,"E14.36.0.4"),sQuery(id+"F0.wireOp",EDGE,"E14.36.0.5"),sQuery(id+"F0.wireOp",EDGE,"E14.36.0.6"),sQuery(id+"F0.wireOp",EDGE,"E14.36.0.7"),sQuery(id+"F0.wireOp",EDGE,"E14.37.0.0"),sQuery(id+"F0.wireOp",EDGE,"E14.37.0.1"),sQuery(id+"F0.wireOp",EDGE,"E14.37.0.2"),sQuery(id+"F0.wireOp",EDGE,"E14.37.0.3"),sQuery(id+"F0.wireOp",EDGE,"E14.37.0.4"),sQuery(id+"F0.wireOp",EDGE,"E14.37.0.5"),sQuery(id+"F0.wireOp",EDGE,"E14.37.0.6"),sQuery(id+"F0.wireOp",EDGE,"E14.37.0.7"),sQuery(id+"F0.wireOp",EDGE,"E14.38.0.0"),sQuery(id+"F0.wireOp",EDGE,"E14.38.0.1"),sQuery(id+"F0.wireOp",EDGE,"E14.38.0.2"),sQuery(id+"F0.wireOp",EDGE,"E14.38.0.3"),sQuery(id+"F0.wireOp",EDGE,"E14.38.0.4"),sQuery(id+"F0.wireOp",EDGE,"E14.38.0.5"),sQuery(id+"F0.wireOp",EDGE,"E14.38.0.6"),sQuery(id+"F0.wireOp",EDGE,"E14.38.0.7"),sQuery(id+"F0.wireOp",EDGE,"E14.39.0.0"),sQuery(id+"F0.wireOp",EDGE,"E14.39.0.1"),sQuery(id+"F0.wireOp",EDGE,"E14.39.0.2"),sQuery(id+"F0.wireOp",EDGE,"E14.39.0.3"),sQuery(id+"F0.wireOp",EDGE,"E14.39.0.4"),sQuery(id+"F0.wireOp",EDGE,"E14.39.0.5"),sQuery(id+"F0.wireOp",EDGE,"E14.39.0.6"),sQuery(id+"F0.wireOp",EDGE,"E14.39.0.7"),sQuery(id+"F0.wireOp",EDGE,"E14.40.0.0"),sQuery(id+"F0.wireOp",EDGE,"E14.40.0.1"),sQuery(id+"F0.wireOp",EDGE,"E14.40.0.2"),sQuery(id+"F0.wireOp",EDGE,"E14.40.0.3"),sQuery(id+"F0.wireOp",EDGE,"E14.40.0.4"),sQuery(id+"F0.wireOp",EDGE,"E14.40.0.5"),sQuery(id+"F0.wireOp",EDGE,"E14.40.0.6"),sQuery(id+"F0.wireOp",EDGE,"E14.40.0.7"),sQuery(id+"F0.wireOp",EDGE,"E14.41.0.0"),sQuery(id+"F0.wireOp",EDGE,"E14.41.0.1"),sQuery(id+"F0.wireOp",EDGE,"E14.41.0.2"),sQuery(id+"F0.wireOp",EDGE,"E14.41.0.3"),sQuery(id+"F0.wireOp",EDGE,"E14.41.0.4"),sQuery(id+"F0.wireOp",EDGE,"E14.41.0.5"),sQuery(id+"F0.wireOp",EDGE,"E14.41.0.6"),sQuery(id+"F0.wireOp",EDGE,"E14.41.0.7"),sQuery(id+"F0.wireOp",EDGE,"E14.42.0.0"),sQuery(id+"F0.wireOp",EDGE,"E14.42.0.1"),sQuery(id+"F0.wireOp",EDGE,"E14.42.0.2"),sQuery(id+"F0.wireOp",EDGE,"E14.42.0.3"),sQuery(id+"F0.wireOp",EDGE,"E14.42.0.4"),sQuery(id+"F0.wireOp",EDGE,"E14.42.0.5"),sQuery(id+"F0.wireOp",EDGE,"E14.42.0.6"),sQuery(id+"F0.wireOp",EDGE,"E14.42.0.7"),sQuery(id+"F0.wireOp",EDGE,"E14.43.0.0"),sQuery(id+"F0.wireOp",EDGE,"E14.43.0.1"),sQuery(id+"F0.wireOp",EDGE,"E14.43.0.2"),sQuery(id+"F0.wireOp",EDGE,"E14.43.0.3"),sQuery(id+"F0.wireOp",EDGE,"E14.43.0.4"),sQuery(id+"F0.wireOp",EDGE,"E14.43.0.5"),sQuery(id+"F0.wireOp",EDGE,"E14.43.0.6"),sQuery(id+"F0.wireOp",EDGE,"E14.43.0.7"),sQuery(id+"F0.wireOp",EDGE,"E14.44.0.0"),sQuery(id+"F0.wireOp",EDGE,"E14.44.0.1"),sQuery(id+"F0.wireOp",EDGE,"E14.44.0.2"),sQuery(id+"F0.wireOp",EDGE,"E14.44.0.3"),sQuery(id+"F0.wireOp",EDGE,"E14.44.0.4"),sQuery(id+"F0.wireOp",EDGE,"E14.44.0.5"),sQuery(id+"F0.wireOp",EDGE,"E14.44.0.6"),sQuery(id+"F0.wireOp",EDGE,"E14.44.0.7"),sQuery(id+"F0.wireOp",EDGE,"E14.45.0.0"),sQuery(id+"F0.wireOp",EDGE,"E14.45.0.1"),sQuery(id+"F0.wireOp",EDGE,"E14.45.0.2"),sQuery(id+"F0.wireOp",EDGE,"E14.45.0.3"),sQuery(id+"F0.wireOp",EDGE,"E14.45.0.4"),sQuery(id+"F0.wireOp",EDGE,"E14.45.0.5"),sQuery(id+"F0.wireOp",EDGE,"E14.45.0.6"),sQuery(id+"F0.wireOp",EDGE,"E14.45.0.7"),sQuery(id+"F0.wireOp",EDGE,"E14.46.0.0"),sQuery(id+"F0.wireOp",EDGE,"E14.46.0.1"),sQuery(id+"F0.wireOp",EDGE,"E14.46.0.2"),sQuery(id+"F0.wireOp",EDGE,"E14.46.0.3"),sQuery(id+"F0.wireOp",EDGE,"E14.46.0.4"),sQuery(id+"F0.wireOp",EDGE,"E14.46.0.5"),sQuery(id+"F0.wireOp",EDGE,"E14.46.0.6"),sQuery(id+"F0.wireOp",EDGE,"E14.46.0.7"),sQuery(id+"F0.wireOp",EDGE,"E14.47.0.0"),sQuery(id+"F0.wireOp",EDGE,"E14.47.0.1"),sQuery(id+"F0.wireOp",EDGE,"E14.47.0.2"),sQuery(id+"F0.wireOp",EDGE,"E14.47.0.3"),sQuery(id+"F0.wireOp",EDGE,"E14.47.0.4"),sQuery(id+"F0.wireOp",EDGE,"E14.47.0.5"),sQuery(id+"F0.wireOp",EDGE,"E14.47.0.6"),sQuery(id+"F0.wireOp",EDGE,"E14.47.0.7"),sQuery(id+"F0.wireOp",EDGE,"E14.48.0.0"),sQuery(id+"F0.wireOp",EDGE,"E14.48.0.1"),sQuery(id+"F0.wireOp",EDGE,"E14.48.0.2"),sQuery(id+"F0.wireOp",EDGE,"E14.48.0.3"),sQuery(id+"F0.wireOp",EDGE,"E14.48.0.4"),sQuery(id+"F0.wireOp",EDGE,"E14.48.0.5"),sQuery(id+"F0.wireOp",EDGE,"E14.48.0.6"),sQuery(id+"F0.wireOp",EDGE,"E14.48.0.7"),sQuery(id+"F0.wireOp",EDGE,"E14.49.0.0"),sQuery(id+"F0.wireOp",EDGE,"E14.49.0.1"),sQuery(id+"F0.wireOp",EDGE,"E14.49.0.2"),sQuery(id+"F0.wireOp",EDGE,"E14.49.0.3"),sQuery(id+"F0.wireOp",EDGE,"E14.49.0.4"),sQuery(id+"F0.wireOp",EDGE,"E14.49.0.5"),sQuery(id+"F0.wireOp",EDGE,"E14.49.0.6"),sQuery(id+"F0.wireOp",EDGE,"E14.49.0.7")])],"isStart":false});
            var sketch = newSketch(context, id + "F2", { "sketchPlane" : qUnion([Q0])});
            skLineSegment(sketch, "E15.bottom", {"start": v(0, 0) * mm, "end": v(50.8, 0) * mm});
            skLineSegment(sketch, "E15.top", {"start": v(0, 12.7) * mm, "end": v(50.8, 12.7) * mm});
            skLineSegment(sketch, "E15.left", {"start": v(0, 0) * mm, "end": v(0, 12.7) * mm});
            skLineSegment(sketch, "E15.right", {"start": v(50.8, 0) * mm, "end": v(50.8, 12.7) * mm});
            skLineSegment(sketch, "E16.bottom", {"start": v(762, 0) * mm, "end": v(711.2, 0) * mm});
            skLineSegment(sketch, "E16.top", {"start": v(762, 12.7) * mm, "end": v(711.2, 12.7) * mm});
            skLineSegment(sketch, "E16.left", {"start": v(762, 0) * mm, "end": v(762, 12.7) * mm});
            skLineSegment(sketch, "E16.right", {"start": v(711.2, 0) * mm, "end": v(711.2, 12.7) * mm});
            skSolve(sketch);
        }
        {
            var Q0;
            Q0=makeQuery(id+"F1.opExtrude","CAP_FACE",FACE,{"disambiguationData":[OSD([sQuery(id+"F0.wireOp",EDGE,"E0.bottom"),sQuery(id+"F0.wireOp",EDGE,"E0.top"),sQuery(id+"F0.wireOp",EDGE,"E0.left"),sQuery(id+"F0.wireOp",EDGE,"E0.right"),sQuery(id+"F0.wireOp",EDGE,"E4"),sQuery(id+"F0.wireOp",EDGE,"E6"),sQuery(id+"F0.wireOp",EDGE,"E7"),sQuery(id+"F0.wireOp",EDGE,"E8"),sQuery(id+"F0.wireOp",EDGE,"E9"),sQuery(id+"F0.wireOp",EDGE,"E10"),sQuery(id+"F0.wireOp",EDGE,"E12.filletArc"),sQuery(id+"F0.wireOp",EDGE,"E13.filletArc"),sQuery(id+"F0.wireOp",EDGE,"E14.1.0.0"),sQuery(id+"F0.wireOp",EDGE,"E14.1.0.1"),sQuery(id+"F0.wireOp",EDGE,"E14.1.0.2"),sQuery(id+"F0.wireOp",EDGE,"E14.1.0.3"),sQuery(id+"F0.wireOp",EDGE,"E14.1.0.4"),sQuery(id+"F0.wireOp",EDGE,"E14.1.0.5"),sQuery(id+"F0.wireOp",EDGE,"E14.1.0.6"),sQuery(id+"F0.wireOp",EDGE,"E14.1.0.7"),sQuery(id+"F0.wireOp",EDGE,"E14.2.0.0"),sQuery(id+"F0.wireOp",EDGE,"E14.2.0.1"),sQuery(id+"F0.wireOp",EDGE,"E14.2.0.2"),sQuery(id+"F0.wireOp",EDGE,"E14.2.0.3"),sQuery(id+"F0.wireOp",EDGE,"E14.2.0.4"),sQuery(id+"F0.wireOp",EDGE,"E14.2.0.5"),sQuery(id+"F0.wireOp",EDGE,"E14.2.0.6"),sQuery(id+"F0.wireOp",EDGE,"E14.2.0.7"),sQuery(id+"F0.wireOp",EDGE,"E14.3.0.0"),sQuery(id+"F0.wireOp",EDGE,"E14.3.0.1"),sQuery(id+"F0.wireOp",EDGE,"E14.3.0.2"),sQuery(id+"F0.wireOp",EDGE,"E14.3.0.3"),sQuery(id+"F0.wireOp",EDGE,"E14.3.0.4"),sQuery(id+"F0.wireOp",EDGE,"E14.3.0.5"),sQuery(id+"F0.wireOp",EDGE,"E14.3.0.6"),sQuery(id+"F0.wireOp",EDGE,"E14.3.0.7"),sQuery(id+"F0.wireOp",EDGE,"E14.4.0.0"),sQuery(id+"F0.wireOp",EDGE,"E14.4.0.1"),sQuery(id+"F0.wireOp",EDGE,"E14.4.0.2"),sQuery(id+"F0.wireOp",EDGE,"E14.4.0.3"),sQuery(id+"F0.wireOp",EDGE,"E14.4.0.4"),sQuery(id+"F0.wireOp",EDGE,"E14.4.0.5"),sQuery(id+"F0.wireOp",EDGE,"E14.4.0.6"),sQuery(id+"F0.wireOp",EDGE,"E14.4.0.7"),sQuery(id+"F0.wireOp",EDGE,"E14.5.0.0"),sQuery(id+"F0.wireOp",EDGE,"E14.5.0.1"),sQuery(id+"F0.wireOp",EDGE,"E14.5.0.2"),sQuery(id+"F0.wireOp",EDGE,"E14.5.0.3"),sQuery(id+"F0.wireOp",EDGE,"E14.5.0.4"),sQuery(id+"F0.wireOp",EDGE,"E14.5.0.5"),sQuery(id+"F0.wireOp",EDGE,"E14.5.0.6"),sQuery(id+"F0.wireOp",EDGE,"E14.5.0.7"),sQuery(id+"F0.wireOp",EDGE,"E14.6.0.0"),sQuery(id+"F0.wireOp",EDGE,"E14.6.0.1"),sQuery(id+"F0.wireOp",EDGE,"E14.6.0.2"),sQuery(id+"F0.wireOp",EDGE,"E14.6.0.3"),sQuery(id+"F0.wireOp",EDGE,"E14.6.0.4"),sQuery(id+"F0.wireOp",EDGE,"E14.6.0.5"),sQuery(id+"F0.wireOp",EDGE,"E14.6.0.6"),sQuery(id+"F0.wireOp",EDGE,"E14.6.0.7"),sQuery(id+"F0.wireOp",EDGE,"E14.7.0.0"),sQuery(id+"F0.wireOp",EDGE,"E14.7.0.1"),sQuery(id+"F0.wireOp",EDGE,"E14.7.0.2"),sQuery(id+"F0.wireOp",EDGE,"E14.7.0.3"),sQuery(id+"F0.wireOp",EDGE,"E14.7.0.4"),sQuery(id+"F0.wireOp",EDGE,"E14.7.0.5"),sQuery(id+"F0.wireOp",EDGE,"E14.7.0.6"),sQuery(id+"F0.wireOp",EDGE,"E14.7.0.7"),sQuery(id+"F0.wireOp",EDGE,"E14.8.0.0"),sQuery(id+"F0.wireOp",EDGE,"E14.8.0.1"),sQuery(id+"F0.wireOp",EDGE,"E14.8.0.2"),sQuery(id+"F0.wireOp",EDGE,"E14.8.0.3"),sQuery(id+"F0.wireOp",EDGE,"E14.8.0.4"),sQuery(id+"F0.wireOp",EDGE,"E14.8.0.5"),sQuery(id+"F0.wireOp",EDGE,"E14.8.0.6"),sQuery(id+"F0.wireOp",EDGE,"E14.8.0.7"),sQuery(id+"F0.wireOp",EDGE,"E14.9.0.0"),sQuery(id+"F0.wireOp",EDGE,"E14.9.0.1"),sQuery(id+"F0.wireOp",EDGE,"E14.9.0.2"),sQuery(id+"F0.wireOp",EDGE,"E14.9.0.3"),sQuery(id+"F0.wireOp",EDGE,"E14.9.0.4"),sQuery(id+"F0.wireOp",EDGE,"E14.9.0.5"),sQuery(id+"F0.wireOp",EDGE,"E14.9.0.6"),sQuery(id+"F0.wireOp",EDGE,"E14.9.0.7"),sQuery(id+"F0.wireOp",EDGE,"E14.10.0.0"),sQuery(id+"F0.wireOp",EDGE,"E14.10.0.1"),sQuery(id+"F0.wireOp",EDGE,"E14.10.0.2"),sQuery(id+"F0.wireOp",EDGE,"E14.10.0.3"),sQuery(id+"F0.wireOp",EDGE,"E14.10.0.4"),sQuery(id+"F0.wireOp",EDGE,"E14.10.0.5"),sQuery(id+"F0.wireOp",EDGE,"E14.10.0.6"),sQuery(id+"F0.wireOp",EDGE,"E14.10.0.7"),sQuery(id+"F0.wireOp",EDGE,"E14.11.0.0"),sQuery(id+"F0.wireOp",EDGE,"E14.11.0.1"),sQuery(id+"F0.wireOp",EDGE,"E14.11.0.2"),sQuery(id+"F0.wireOp",EDGE,"E14.11.0.3"),sQuery(id+"F0.wireOp",EDGE,"E14.11.0.4"),sQuery(id+"F0.wireOp",EDGE,"E14.11.0.5"),sQuery(id+"F0.wireOp",EDGE,"E14.11.0.6"),sQuery(id+"F0.wireOp",EDGE,"E14.11.0.7"),sQuery(id+"F0.wireOp",EDGE,"E14.12.0.0"),sQuery(id+"F0.wireOp",EDGE,"E14.12.0.1"),sQuery(id+"F0.wireOp",EDGE,"E14.12.0.2"),sQuery(id+"F0.wireOp",EDGE,"E14.12.0.3"),sQuery(id+"F0.wireOp",EDGE,"E14.12.0.4"),sQuery(id+"F0.wireOp",EDGE,"E14.12.0.5"),sQuery(id+"F0.wireOp",EDGE,"E14.12.0.6"),sQuery(id+"F0.wireOp",EDGE,"E14.12.0.7"),sQuery(id+"F0.wireOp",EDGE,"E14.13.0.0"),sQuery(id+"F0.wireOp",EDGE,"E14.13.0.1"),sQuery(id+"F0.wireOp",EDGE,"E14.13.0.2"),sQuery(id+"F0.wireOp",EDGE,"E14.13.0.3"),sQuery(id+"F0.wireOp",EDGE,"E14.13.0.4"),sQuery(id+"F0.wireOp",EDGE,"E14.13.0.5"),sQuery(id+"F0.wireOp",EDGE,"E14.13.0.6"),sQuery(id+"F0.wireOp",EDGE,"E14.13.0.7"),sQuery(id+"F0.wireOp",EDGE,"E14.14.0.0"),sQuery(id+"F0.wireOp",EDGE,"E14.14.0.1"),sQuery(id+"F0.wireOp",EDGE,"E14.14.0.2"),sQuery(id+"F0.wireOp",EDGE,"E14.14.0.3"),sQuery(id+"F0.wireOp",EDGE,"E14.14.0.4"),sQuery(id+"F0.wireOp",EDGE,"E14.14.0.5"),sQuery(id+"F0.wireOp",EDGE,"E14.14.0.6"),sQuery(id+"F0.wireOp",EDGE,"E14.14.0.7"),sQuery(id+"F0.wireOp",EDGE,"E14.15.0.0"),sQuery(id+"F0.wireOp",EDGE,"E14.15.0.1"),sQuery(id+"F0.wireOp",EDGE,"E14.15.0.2"),sQuery(id+"F0.wireOp",EDGE,"E14.15.0.3"),sQuery(id+"F0.wireOp",EDGE,"E14.15.0.4"),sQuery(id+"F0.wireOp",EDGE,"E14.15.0.5"),sQuery(id+"F0.wireOp",EDGE,"E14.15.0.6"),sQuery(id+"F0.wireOp",EDGE,"E14.15.0.7"),sQuery(id+"F0.wireOp",EDGE,"E14.16.0.0"),sQuery(id+"F0.wireOp",EDGE,"E14.16.0.1"),sQuery(id+"F0.wireOp",EDGE,"E14.16.0.2"),sQuery(id+"F0.wireOp",EDGE,"E14.16.0.3"),sQuery(id+"F0.wireOp",EDGE,"E14.16.0.4"),sQuery(id+"F0.wireOp",EDGE,"E14.16.0.5"),sQuery(id+"F0.wireOp",EDGE,"E14.16.0.6"),sQuery(id+"F0.wireOp",EDGE,"E14.16.0.7"),sQuery(id+"F0.wireOp",EDGE,"E14.17.0.0"),sQuery(id+"F0.wireOp",EDGE,"E14.17.0.1"),sQuery(id+"F0.wireOp",EDGE,"E14.17.0.2"),sQuery(id+"F0.wireOp",EDGE,"E14.17.0.3"),sQuery(id+"F0.wireOp",EDGE,"E14.17.0.4"),sQuery(id+"F0.wireOp",EDGE,"E14.17.0.5"),sQuery(id+"F0.wireOp",EDGE,"E14.17.0.6"),sQuery(id+"F0.wireOp",EDGE,"E14.17.0.7"),sQuery(id+"F0.wireOp",EDGE,"E14.18.0.0"),sQuery(id+"F0.wireOp",EDGE,"E14.18.0.1"),sQuery(id+"F0.wireOp",EDGE,"E14.18.0.2"),sQuery(id+"F0.wireOp",EDGE,"E14.18.0.3"),sQuery(id+"F0.wireOp",EDGE,"E14.18.0.4"),sQuery(id+"F0.wireOp",EDGE,"E14.18.0.5"),sQuery(id+"F0.wireOp",EDGE,"E14.18.0.6"),sQuery(id+"F0.wireOp",EDGE,"E14.18.0.7"),sQuery(id+"F0.wireOp",EDGE,"E14.19.0.0"),sQuery(id+"F0.wireOp",EDGE,"E14.19.0.1"),sQuery(id+"F0.wireOp",EDGE,"E14.19.0.2"),sQuery(id+"F0.wireOp",EDGE,"E14.19.0.3"),sQuery(id+"F0.wireOp",EDGE,"E14.19.0.4"),sQuery(id+"F0.wireOp",EDGE,"E14.19.0.5"),sQuery(id+"F0.wireOp",EDGE,"E14.19.0.6"),sQuery(id+"F0.wireOp",EDGE,"E14.19.0.7"),sQuery(id+"F0.wireOp",EDGE,"E14.20.0.0"),sQuery(id+"F0.wireOp",EDGE,"E14.20.0.1"),sQuery(id+"F0.wireOp",EDGE,"E14.20.0.2"),sQuery(id+"F0.wireOp",EDGE,"E14.20.0.3"),sQuery(id+"F0.wireOp",EDGE,"E14.20.0.4"),sQuery(id+"F0.wireOp",EDGE,"E14.20.0.5"),sQuery(id+"F0.wireOp",EDGE,"E14.20.0.6"),sQuery(id+"F0.wireOp",EDGE,"E14.20.0.7"),sQuery(id+"F0.wireOp",EDGE,"E14.21.0.0"),sQuery(id+"F0.wireOp",EDGE,"E14.21.0.1"),sQuery(id+"F0.wireOp",EDGE,"E14.21.0.2"),sQuery(id+"F0.wireOp",EDGE,"E14.21.0.3"),sQuery(id+"F0.wireOp",EDGE,"E14.21.0.4"),sQuery(id+"F0.wireOp",EDGE,"E14.21.0.5"),sQuery(id+"F0.wireOp",EDGE,"E14.21.0.6"),sQuery(id+"F0.wireOp",EDGE,"E14.21.0.7"),sQuery(id+"F0.wireOp",EDGE,"E14.22.0.0"),sQuery(id+"F0.wireOp",EDGE,"E14.22.0.1"),sQuery(id+"F0.wireOp",EDGE,"E14.22.0.2"),sQuery(id+"F0.wireOp",EDGE,"E14.22.0.3"),sQuery(id+"F0.wireOp",EDGE,"E14.22.0.4"),sQuery(id+"F0.wireOp",EDGE,"E14.22.0.5"),sQuery(id+"F0.wireOp",EDGE,"E14.22.0.6"),sQuery(id+"F0.wireOp",EDGE,"E14.22.0.7"),sQuery(id+"F0.wireOp",EDGE,"E14.23.0.0"),sQuery(id+"F0.wireOp",EDGE,"E14.23.0.1"),sQuery(id+"F0.wireOp",EDGE,"E14.23.0.2"),sQuery(id+"F0.wireOp",EDGE,"E14.23.0.3"),sQuery(id+"F0.wireOp",EDGE,"E14.23.0.4"),sQuery(id+"F0.wireOp",EDGE,"E14.23.0.5"),sQuery(id+"F0.wireOp",EDGE,"E14.23.0.6"),sQuery(id+"F0.wireOp",EDGE,"E14.23.0.7"),sQuery(id+"F0.wireOp",EDGE,"E14.24.0.0"),sQuery(id+"F0.wireOp",EDGE,"E14.24.0.1"),sQuery(id+"F0.wireOp",EDGE,"E14.24.0.2"),sQuery(id+"F0.wireOp",EDGE,"E14.24.0.3"),sQuery(id+"F0.wireOp",EDGE,"E14.24.0.4"),sQuery(id+"F0.wireOp",EDGE,"E14.24.0.5"),sQuery(id+"F0.wireOp",EDGE,"E14.24.0.6"),sQuery(id+"F0.wireOp",EDGE,"E14.24.0.7"),sQuery(id+"F0.wireOp",EDGE,"E14.25.0.0"),sQuery(id+"F0.wireOp",EDGE,"E14.25.0.1"),sQuery(id+"F0.wireOp",EDGE,"E14.25.0.2"),sQuery(id+"F0.wireOp",EDGE,"E14.25.0.3"),sQuery(id+"F0.wireOp",EDGE,"E14.25.0.4"),sQuery(id+"F0.wireOp",EDGE,"E14.25.0.5"),sQuery(id+"F0.wireOp",EDGE,"E14.25.0.6"),sQuery(id+"F0.wireOp",EDGE,"E14.25.0.7"),sQuery(id+"F0.wireOp",EDGE,"E14.26.0.0"),sQuery(id+"F0.wireOp",EDGE,"E14.26.0.1"),sQuery(id+"F0.wireOp",EDGE,"E14.26.0.2"),sQuery(id+"F0.wireOp",EDGE,"E14.26.0.3"),sQuery(id+"F0.wireOp",EDGE,"E14.26.0.4"),sQuery(id+"F0.wireOp",EDGE,"E14.26.0.5"),sQuery(id+"F0.wireOp",EDGE,"E14.26.0.6"),sQuery(id+"F0.wireOp",EDGE,"E14.26.0.7"),sQuery(id+"F0.wireOp",EDGE,"E14.27.0.0"),sQuery(id+"F0.wireOp",EDGE,"E14.27.0.1"),sQuery(id+"F0.wireOp",EDGE,"E14.27.0.2"),sQuery(id+"F0.wireOp",EDGE,"E14.27.0.3"),sQuery(id+"F0.wireOp",EDGE,"E14.27.0.4"),sQuery(id+"F0.wireOp",EDGE,"E14.27.0.5"),sQuery(id+"F0.wireOp",EDGE,"E14.27.0.6"),sQuery(id+"F0.wireOp",EDGE,"E14.27.0.7"),sQuery(id+"F0.wireOp",EDGE,"E14.28.0.0"),sQuery(id+"F0.wireOp",EDGE,"E14.28.0.1"),sQuery(id+"F0.wireOp",EDGE,"E14.28.0.2"),sQuery(id+"F0.wireOp",EDGE,"E14.28.0.3"),sQuery(id+"F0.wireOp",EDGE,"E14.28.0.4"),sQuery(id+"F0.wireOp",EDGE,"E14.28.0.5"),sQuery(id+"F0.wireOp",EDGE,"E14.28.0.6"),sQuery(id+"F0.wireOp",EDGE,"E14.28.0.7"),sQuery(id+"F0.wireOp",EDGE,"E14.29.0.0"),sQuery(id+"F0.wireOp",EDGE,"E14.29.0.1"),sQuery(id+"F0.wireOp",EDGE,"E14.29.0.2"),sQuery(id+"F0.wireOp",EDGE,"E14.29.0.3"),sQuery(id+"F0.wireOp",EDGE,"E14.29.0.4"),sQuery(id+"F0.wireOp",EDGE,"E14.29.0.5"),sQuery(id+"F0.wireOp",EDGE,"E14.29.0.6"),sQuery(id+"F0.wireOp",EDGE,"E14.29.0.7"),sQuery(id+"F0.wireOp",EDGE,"E14.30.0.0"),sQuery(id+"F0.wireOp",EDGE,"E14.30.0.1"),sQuery(id+"F0.wireOp",EDGE,"E14.30.0.2"),sQuery(id+"F0.wireOp",EDGE,"E14.30.0.3"),sQuery(id+"F0.wireOp",EDGE,"E14.30.0.4"),sQuery(id+"F0.wireOp",EDGE,"E14.30.0.5"),sQuery(id+"F0.wireOp",EDGE,"E14.30.0.6"),sQuery(id+"F0.wireOp",EDGE,"E14.30.0.7"),sQuery(id+"F0.wireOp",EDGE,"E14.31.0.0"),sQuery(id+"F0.wireOp",EDGE,"E14.31.0.1"),sQuery(id+"F0.wireOp",EDGE,"E14.31.0.2"),sQuery(id+"F0.wireOp",EDGE,"E14.31.0.3"),sQuery(id+"F0.wireOp",EDGE,"E14.31.0.4"),sQuery(id+"F0.wireOp",EDGE,"E14.31.0.5"),sQuery(id+"F0.wireOp",EDGE,"E14.31.0.6"),sQuery(id+"F0.wireOp",EDGE,"E14.31.0.7"),sQuery(id+"F0.wireOp",EDGE,"E14.32.0.0"),sQuery(id+"F0.wireOp",EDGE,"E14.32.0.1"),sQuery(id+"F0.wireOp",EDGE,"E14.32.0.2"),sQuery(id+"F0.wireOp",EDGE,"E14.32.0.3"),sQuery(id+"F0.wireOp",EDGE,"E14.32.0.4"),sQuery(id+"F0.wireOp",EDGE,"E14.32.0.5"),sQuery(id+"F0.wireOp",EDGE,"E14.32.0.6"),sQuery(id+"F0.wireOp",EDGE,"E14.32.0.7"),sQuery(id+"F0.wireOp",EDGE,"E14.33.0.0"),sQuery(id+"F0.wireOp",EDGE,"E14.33.0.1"),sQuery(id+"F0.wireOp",EDGE,"E14.33.0.2"),sQuery(id+"F0.wireOp",EDGE,"E14.33.0.3"),sQuery(id+"F0.wireOp",EDGE,"E14.33.0.4"),sQuery(id+"F0.wireOp",EDGE,"E14.33.0.5"),sQuery(id+"F0.wireOp",EDGE,"E14.33.0.6"),sQuery(id+"F0.wireOp",EDGE,"E14.33.0.7"),sQuery(id+"F0.wireOp",EDGE,"E14.34.0.0"),sQuery(id+"F0.wireOp",EDGE,"E14.34.0.1"),sQuery(id+"F0.wireOp",EDGE,"E14.34.0.2"),sQuery(id+"F0.wireOp",EDGE,"E14.34.0.3"),sQuery(id+"F0.wireOp",EDGE,"E14.34.0.4"),sQuery(id+"F0.wireOp",EDGE,"E14.34.0.5"),sQuery(id+"F0.wireOp",EDGE,"E14.34.0.6"),sQuery(id+"F0.wireOp",EDGE,"E14.34.0.7"),sQuery(id+"F0.wireOp",EDGE,"E14.35.0.0"),sQuery(id+"F0.wireOp",EDGE,"E14.35.0.1"),sQuery(id+"F0.wireOp",EDGE,"E14.35.0.2"),sQuery(id+"F0.wireOp",EDGE,"E14.35.0.3"),sQuery(id+"F0.wireOp",EDGE,"E14.35.0.4"),sQuery(id+"F0.wireOp",EDGE,"E14.35.0.5"),sQuery(id+"F0.wireOp",EDGE,"E14.35.0.6"),sQuery(id+"F0.wireOp",EDGE,"E14.35.0.7"),sQuery(id+"F0.wireOp",EDGE,"E14.36.0.0"),sQuery(id+"F0.wireOp",EDGE,"E14.36.0.1"),sQuery(id+"F0.wireOp",EDGE,"E14.36.0.2"),sQuery(id+"F0.wireOp",EDGE,"E14.36.0.3"),sQuery(id+"F0.wireOp",EDGE,"E14.36.0.4"),sQuery(id+"F0.wireOp",EDGE,"E14.36.0.5"),sQuery(id+"F0.wireOp",EDGE,"E14.36.0.6"),sQuery(id+"F0.wireOp",EDGE,"E14.36.0.7"),sQuery(id+"F0.wireOp",EDGE,"E14.37.0.0"),sQuery(id+"F0.wireOp",EDGE,"E14.37.0.1"),sQuery(id+"F0.wireOp",EDGE,"E14.37.0.2"),sQuery(id+"F0.wireOp",EDGE,"E14.37.0.3"),sQuery(id+"F0.wireOp",EDGE,"E14.37.0.4"),sQuery(id+"F0.wireOp",EDGE,"E14.37.0.5"),sQuery(id+"F0.wireOp",EDGE,"E14.37.0.6"),sQuery(id+"F0.wireOp",EDGE,"E14.37.0.7"),sQuery(id+"F0.wireOp",EDGE,"E14.38.0.0"),sQuery(id+"F0.wireOp",EDGE,"E14.38.0.1"),sQuery(id+"F0.wireOp",EDGE,"E14.38.0.2"),sQuery(id+"F0.wireOp",EDGE,"E14.38.0.3"),sQuery(id+"F0.wireOp",EDGE,"E14.38.0.4"),sQuery(id+"F0.wireOp",EDGE,"E14.38.0.5"),sQuery(id+"F0.wireOp",EDGE,"E14.38.0.6"),sQuery(id+"F0.wireOp",EDGE,"E14.38.0.7"),sQuery(id+"F0.wireOp",EDGE,"E14.39.0.0"),sQuery(id+"F0.wireOp",EDGE,"E14.39.0.1"),sQuery(id+"F0.wireOp",EDGE,"E14.39.0.2"),sQuery(id+"F0.wireOp",EDGE,"E14.39.0.3"),sQuery(id+"F0.wireOp",EDGE,"E14.39.0.4"),sQuery(id+"F0.wireOp",EDGE,"E14.39.0.5"),sQuery(id+"F0.wireOp",EDGE,"E14.39.0.6"),sQuery(id+"F0.wireOp",EDGE,"E14.39.0.7"),sQuery(id+"F0.wireOp",EDGE,"E14.40.0.0"),sQuery(id+"F0.wireOp",EDGE,"E14.40.0.1"),sQuery(id+"F0.wireOp",EDGE,"E14.40.0.2"),sQuery(id+"F0.wireOp",EDGE,"E14.40.0.3"),sQuery(id+"F0.wireOp",EDGE,"E14.40.0.4"),sQuery(id+"F0.wireOp",EDGE,"E14.40.0.5"),sQuery(id+"F0.wireOp",EDGE,"E14.40.0.6"),sQuery(id+"F0.wireOp",EDGE,"E14.40.0.7"),sQuery(id+"F0.wireOp",EDGE,"E14.41.0.0"),sQuery(id+"F0.wireOp",EDGE,"E14.41.0.1"),sQuery(id+"F0.wireOp",EDGE,"E14.41.0.2"),sQuery(id+"F0.wireOp",EDGE,"E14.41.0.3"),sQuery(id+"F0.wireOp",EDGE,"E14.41.0.4"),sQuery(id+"F0.wireOp",EDGE,"E14.41.0.5"),sQuery(id+"F0.wireOp",EDGE,"E14.41.0.6"),sQuery(id+"F0.wireOp",EDGE,"E14.41.0.7"),sQuery(id+"F0.wireOp",EDGE,"E14.42.0.0"),sQuery(id+"F0.wireOp",EDGE,"E14.42.0.1"),sQuery(id+"F0.wireOp",EDGE,"E14.42.0.2"),sQuery(id+"F0.wireOp",EDGE,"E14.42.0.3"),sQuery(id+"F0.wireOp",EDGE,"E14.42.0.4"),sQuery(id+"F0.wireOp",EDGE,"E14.42.0.5"),sQuery(id+"F0.wireOp",EDGE,"E14.42.0.6"),sQuery(id+"F0.wireOp",EDGE,"E14.42.0.7"),sQuery(id+"F0.wireOp",EDGE,"E14.43.0.0"),sQuery(id+"F0.wireOp",EDGE,"E14.43.0.1"),sQuery(id+"F0.wireOp",EDGE,"E14.43.0.2"),sQuery(id+"F0.wireOp",EDGE,"E14.43.0.3"),sQuery(id+"F0.wireOp",EDGE,"E14.43.0.4"),sQuery(id+"F0.wireOp",EDGE,"E14.43.0.5"),sQuery(id+"F0.wireOp",EDGE,"E14.43.0.6"),sQuery(id+"F0.wireOp",EDGE,"E14.43.0.7"),sQuery(id+"F0.wireOp",EDGE,"E14.44.0.0"),sQuery(id+"F0.wireOp",EDGE,"E14.44.0.1"),sQuery(id+"F0.wireOp",EDGE,"E14.44.0.2"),sQuery(id+"F0.wireOp",EDGE,"E14.44.0.3"),sQuery(id+"F0.wireOp",EDGE,"E14.44.0.4"),sQuery(id+"F0.wireOp",EDGE,"E14.44.0.5"),sQuery(id+"F0.wireOp",EDGE,"E14.44.0.6"),sQuery(id+"F0.wireOp",EDGE,"E14.44.0.7"),sQuery(id+"F0.wireOp",EDGE,"E14.45.0.0"),sQuery(id+"F0.wireOp",EDGE,"E14.45.0.1"),sQuery(id+"F0.wireOp",EDGE,"E14.45.0.2"),sQuery(id+"F0.wireOp",EDGE,"E14.45.0.3"),sQuery(id+"F0.wireOp",EDGE,"E14.45.0.4"),sQuery(id+"F0.wireOp",EDGE,"E14.45.0.5"),sQuery(id+"F0.wireOp",EDGE,"E14.45.0.6"),sQuery(id+"F0.wireOp",EDGE,"E14.45.0.7"),sQuery(id+"F0.wireOp",EDGE,"E14.46.0.0"),sQuery(id+"F0.wireOp",EDGE,"E14.46.0.1"),sQuery(id+"F0.wireOp",EDGE,"E14.46.0.2"),sQuery(id+"F0.wireOp",EDGE,"E14.46.0.3"),sQuery(id+"F0.wireOp",EDGE,"E14.46.0.4"),sQuery(id+"F0.wireOp",EDGE,"E14.46.0.5"),sQuery(id+"F0.wireOp",EDGE,"E14.46.0.6"),sQuery(id+"F0.wireOp",EDGE,"E14.46.0.7"),sQuery(id+"F0.wireOp",EDGE,"E14.47.0.0"),sQuery(id+"F0.wireOp",EDGE,"E14.47.0.1"),sQuery(id+"F0.wireOp",EDGE,"E14.47.0.2"),sQuery(id+"F0.wireOp",EDGE,"E14.47.0.3"),sQuery(id+"F0.wireOp",EDGE,"E14.47.0.4"),sQuery(id+"F0.wireOp",EDGE,"E14.47.0.5"),sQuery(id+"F0.wireOp",EDGE,"E14.47.0.6"),sQuery(id+"F0.wireOp",EDGE,"E14.47.0.7"),sQuery(id+"F0.wireOp",EDGE,"E14.48.0.0"),sQuery(id+"F0.wireOp",EDGE,"E14.48.0.1"),sQuery(id+"F0.wireOp",EDGE,"E14.48.0.2"),sQuery(id+"F0.wireOp",EDGE,"E14.48.0.3"),sQuery(id+"F0.wireOp",EDGE,"E14.48.0.4"),sQuery(id+"F0.wireOp",EDGE,"E14.48.0.5"),sQuery(id+"F0.wireOp",EDGE,"E14.48.0.6"),sQuery(id+"F0.wireOp",EDGE,"E14.48.0.7"),sQuery(id+"F0.wireOp",EDGE,"E14.49.0.0"),sQuery(id+"F0.wireOp",EDGE,"E14.49.0.1"),sQuery(id+"F0.wireOp",EDGE,"E14.49.0.2"),sQuery(id+"F0.wireOp",EDGE,"E14.49.0.3"),sQuery(id+"F0.wireOp",EDGE,"E14.49.0.4"),sQuery(id+"F0.wireOp",EDGE,"E14.49.0.5"),sQuery(id+"F0.wireOp",EDGE,"E14.49.0.6"),sQuery(id+"F0.wireOp",EDGE,"E14.49.0.7")])],"isStart":true});
            var sketch = newSketch(context, id + "F3", { "sketchPlane" : qUnion([Q0])});
            skLineSegment(sketch, "E17.bottom", {"start": v(-762, 0) * mm, "end": v(-711.2, 0) * mm});
            skLineSegment(sketch, "E17.top", {"start": v(-762, 12.7) * mm, "end": v(-711.2, 12.7) * mm});
            skLineSegment(sketch, "E17.left", {"start": v(-762, 0) * mm, "end": v(-762, 12.7) * mm});
            skLineSegment(sketch, "E17.right", {"start": v(-711.2, 0) * mm, "end": v(-711.2, 12.7) * mm});
            skLineSegment(sketch, "E18.bottom", {"start": v(0, 0) * mm, "end": v(-50.8, 0) * mm});
            skLineSegment(sketch, "E18.top", {"start": v(0, 12.7) * mm, "end": v(-50.8, 12.7) * mm});
            skLineSegment(sketch, "E18.left", {"start": v(0, 0) * mm, "end": v(0, 12.7) * mm});
            skLineSegment(sketch, "E18.right", {"start": v(-50.8, 0) * mm, "end": v(-50.8, 12.7) * mm});
            skSolve(sketch);
        }
        {
            var Q0;
            Q0 = qSketchRegion(id + "F2", true);
            var Q1;
            Q1 = qSketchRegion(id + "F3", true);
            extrude(context, id + "F4", {"entities" : qUnion([Q0, Q1]), "operationType" : NewBodyOperationType.ADD, "depth" : 25.4 * mm, "hasSecondDirection" : true, "secondDirectionOppositeDirection" : true, "secondDirectionDepth" : 25.4 * mm});
        }
        {
            var Q0;
            Q0=makeQuery(id+"F4.opExtrude","SWEPT_FACE",FACE,{"disambiguationData":[OSD([sQuery(id+"F3.wireOp",EDGE,"E18.top")])]});
            var sketch = newSketch(context, id + "F5", { "sketchPlane" : qUnion([Q0])});
            skPoint(sketch, "E19", {"position": v(6.35, 12.7) * mm});
            skPoint(sketch, "E20", {"position": v(44.45, 12.7) * mm});
            skLineSegment(sketch, "E21", {"start": v(0, 12.7) * mm, "end": v(0, -165.1) * mm});
            skSolve(sketch);
        }
        {
            var Q0;
            Q0=makeQuery(id+"F4.opExtrude","SWEPT_FACE",FACE,{"disambiguationData":[OSD([sQuery(id+"F2.wireOp",EDGE,"E15.top")])]});
            var sketch = newSketch(context, id + "F6", { "sketchPlane" : qUnion([Q0])});
            skPoint(sketch, "E22", {"position": v(6.35, -165.1) * mm});
            skPoint(sketch, "E23", {"position": v(44.45, -165.1) * mm});
            skSolve(sketch);
        }
        {
            var Q0;
            Q0=makeQuery(id+"F4.opExtrude","SWEPT_FACE",FACE,{"disambiguationData":[OSD([sQuery(id+"F3.wireOp",EDGE,"E17.top")])]});
            var sketch = newSketch(context, id + "F7", { "sketchPlane" : qUnion([Q0])});
            skPoint(sketch, "E24", {"position": v(717.55, 12.7) * mm});
            skPoint(sketch, "E25", {"position": v(755.65, 12.7) * mm});
            skPoint(sketch, "E26.MirrorP", {"position": v(717.55, -165.94) * mm});
            skPoint(sketch, "E27.MirrorP", {"position": v(755.65, -165.94) * mm});
            skSolve(sketch);
        }
        {
            var Q0;
            Q0=sQuery(id+"F5.wireOp",VERTEX,"E19");
            var Q1;
            Q1=sQuery(id+"F5.wireOp",VERTEX,"E20");
            var Q2;
            Q2=sQuery(id+"F6.wireOp",VERTEX,"E22");
            var Q3;
            Q3=sQuery(id+"F6.wireOp",VERTEX,"E23");
            var Q4;
            Q4=sQuery(id+"F7.wireOp",VERTEX,"E24");
            var Q5;
            Q5=sQuery(id+"F7.wireOp",VERTEX,"E25");
            var Q6;
            Q6=sQuery(id+"F7.wireOp",VERTEX,"E26.MirrorP");
            var Q7;
            Q7=sQuery(id+"F7.wireOp",VERTEX,"E27.MirrorP");
            var Q8;
            Q8=makeQuery(id+"F1.opExtrude","SWEPT_BODY",BODY,{"disambiguationData":[OSD([sQuery(id+"F0.wireOp",EDGE,"E0.bottom"),sQuery(id+"F0.wireOp",EDGE,"E0.top"),sQuery(id+"F0.wireOp",EDGE,"E0.left"),sQuery(id+"F0.wireOp",EDGE,"E0.right"),sQuery(id+"F0.wireOp",EDGE,"E4"),sQuery(id+"F0.wireOp",EDGE,"E6"),sQuery(id+"F0.wireOp",EDGE,"E7"),sQuery(id+"F0.wireOp",EDGE,"E8"),sQuery(id+"F0.wireOp",EDGE,"E9"),sQuery(id+"F0.wireOp",EDGE,"E10"),sQuery(id+"F0.wireOp",EDGE,"E12.filletArc"),sQuery(id+"F0.wireOp",EDGE,"E13.filletArc"),sQuery(id+"F0.wireOp",EDGE,"E14.1.0.0"),sQuery(id+"F0.wireOp",EDGE,"E14.1.0.1"),sQuery(id+"F0.wireOp",EDGE,"E14.1.0.2"),sQuery(id+"F0.wireOp",EDGE,"E14.1.0.3"),sQuery(id+"F0.wireOp",EDGE,"E14.1.0.4"),sQuery(id+"F0.wireOp",EDGE,"E14.1.0.5"),sQuery(id+"F0.wireOp",EDGE,"E14.1.0.6"),sQuery(id+"F0.wireOp",EDGE,"E14.1.0.7"),sQuery(id+"F0.wireOp",EDGE,"E14.2.0.0"),sQuery(id+"F0.wireOp",EDGE,"E14.2.0.1"),sQuery(id+"F0.wireOp",EDGE,"E14.2.0.2"),sQuery(id+"F0.wireOp",EDGE,"E14.2.0.3"),sQuery(id+"F0.wireOp",EDGE,"E14.2.0.4"),sQuery(id+"F0.wireOp",EDGE,"E14.2.0.5"),sQuery(id+"F0.wireOp",EDGE,"E14.2.0.6"),sQuery(id+"F0.wireOp",EDGE,"E14.2.0.7"),sQuery(id+"F0.wireOp",EDGE,"E14.3.0.0"),sQuery(id+"F0.wireOp",EDGE,"E14.3.0.1"),sQuery(id+"F0.wireOp",EDGE,"E14.3.0.2"),sQuery(id+"F0.wireOp",EDGE,"E14.3.0.3"),sQuery(id+"F0.wireOp",EDGE,"E14.3.0.4"),sQuery(id+"F0.wireOp",EDGE,"E14.3.0.5"),sQuery(id+"F0.wireOp",EDGE,"E14.3.0.6"),sQuery(id+"F0.wireOp",EDGE,"E14.3.0.7"),sQuery(id+"F0.wireOp",EDGE,"E14.4.0.0"),sQuery(id+"F0.wireOp",EDGE,"E14.4.0.1"),sQuery(id+"F0.wireOp",EDGE,"E14.4.0.2"),sQuery(id+"F0.wireOp",EDGE,"E14.4.0.3"),sQuery(id+"F0.wireOp",EDGE,"E14.4.0.4"),sQuery(id+"F0.wireOp",EDGE,"E14.4.0.5"),sQuery(id+"F0.wireOp",EDGE,"E14.4.0.6"),sQuery(id+"F0.wireOp",EDGE,"E14.4.0.7"),sQuery(id+"F0.wireOp",EDGE,"E14.5.0.0"),sQuery(id+"F0.wireOp",EDGE,"E14.5.0.1"),sQuery(id+"F0.wireOp",EDGE,"E14.5.0.2"),sQuery(id+"F0.wireOp",EDGE,"E14.5.0.3"),sQuery(id+"F0.wireOp",EDGE,"E14.5.0.4"),sQuery(id+"F0.wireOp",EDGE,"E14.5.0.5"),sQuery(id+"F0.wireOp",EDGE,"E14.5.0.6"),sQuery(id+"F0.wireOp",EDGE,"E14.5.0.7"),sQuery(id+"F0.wireOp",EDGE,"E14.6.0.0"),sQuery(id+"F0.wireOp",EDGE,"E14.6.0.1"),sQuery(id+"F0.wireOp",EDGE,"E14.6.0.2"),sQuery(id+"F0.wireOp",EDGE,"E14.6.0.3"),sQuery(id+"F0.wireOp",EDGE,"E14.6.0.4"),sQuery(id+"F0.wireOp",EDGE,"E14.6.0.5"),sQuery(id+"F0.wireOp",EDGE,"E14.6.0.6"),sQuery(id+"F0.wireOp",EDGE,"E14.6.0.7"),sQuery(id+"F0.wireOp",EDGE,"E14.7.0.0"),sQuery(id+"F0.wireOp",EDGE,"E14.7.0.1"),sQuery(id+"F0.wireOp",EDGE,"E14.7.0.2"),sQuery(id+"F0.wireOp",EDGE,"E14.7.0.3"),sQuery(id+"F0.wireOp",EDGE,"E14.7.0.4"),sQuery(id+"F0.wireOp",EDGE,"E14.7.0.5"),sQuery(id+"F0.wireOp",EDGE,"E14.7.0.6"),sQuery(id+"F0.wireOp",EDGE,"E14.7.0.7"),sQuery(id+"F0.wireOp",EDGE,"E14.8.0.0"),sQuery(id+"F0.wireOp",EDGE,"E14.8.0.1"),sQuery(id+"F0.wireOp",EDGE,"E14.8.0.2"),sQuery(id+"F0.wireOp",EDGE,"E14.8.0.3"),sQuery(id+"F0.wireOp",EDGE,"E14.8.0.4"),sQuery(id+"F0.wireOp",EDGE,"E14.8.0.5"),sQuery(id+"F0.wireOp",EDGE,"E14.8.0.6"),sQuery(id+"F0.wireOp",EDGE,"E14.8.0.7"),sQuery(id+"F0.wireOp",EDGE,"E14.9.0.0"),sQuery(id+"F0.wireOp",EDGE,"E14.9.0.1"),sQuery(id+"F0.wireOp",EDGE,"E14.9.0.2"),sQuery(id+"F0.wireOp",EDGE,"E14.9.0.3"),sQuery(id+"F0.wireOp",EDGE,"E14.9.0.4"),sQuery(id+"F0.wireOp",EDGE,"E14.9.0.5"),sQuery(id+"F0.wireOp",EDGE,"E14.9.0.6"),sQuery(id+"F0.wireOp",EDGE,"E14.9.0.7"),sQuery(id+"F0.wireOp",EDGE,"E14.10.0.0"),sQuery(id+"F0.wireOp",EDGE,"E14.10.0.1"),sQuery(id+"F0.wireOp",EDGE,"E14.10.0.2"),sQuery(id+"F0.wireOp",EDGE,"E14.10.0.3"),sQuery(id+"F0.wireOp",EDGE,"E14.10.0.4"),sQuery(id+"F0.wireOp",EDGE,"E14.10.0.5"),sQuery(id+"F0.wireOp",EDGE,"E14.10.0.6"),sQuery(id+"F0.wireOp",EDGE,"E14.10.0.7"),sQuery(id+"F0.wireOp",EDGE,"E14.11.0.0"),sQuery(id+"F0.wireOp",EDGE,"E14.11.0.1"),sQuery(id+"F0.wireOp",EDGE,"E14.11.0.2"),sQuery(id+"F0.wireOp",EDGE,"E14.11.0.3"),sQuery(id+"F0.wireOp",EDGE,"E14.11.0.4"),sQuery(id+"F0.wireOp",EDGE,"E14.11.0.5"),sQuery(id+"F0.wireOp",EDGE,"E14.11.0.6"),sQuery(id+"F0.wireOp",EDGE,"E14.11.0.7"),sQuery(id+"F0.wireOp",EDGE,"E14.12.0.0"),sQuery(id+"F0.wireOp",EDGE,"E14.12.0.1"),sQuery(id+"F0.wireOp",EDGE,"E14.12.0.2"),sQuery(id+"F0.wireOp",EDGE,"E14.12.0.3"),sQuery(id+"F0.wireOp",EDGE,"E14.12.0.4"),sQuery(id+"F0.wireOp",EDGE,"E14.12.0.5"),sQuery(id+"F0.wireOp",EDGE,"E14.12.0.6"),sQuery(id+"F0.wireOp",EDGE,"E14.12.0.7"),sQuery(id+"F0.wireOp",EDGE,"E14.13.0.0"),sQuery(id+"F0.wireOp",EDGE,"E14.13.0.1"),sQuery(id+"F0.wireOp",EDGE,"E14.13.0.2"),sQuery(id+"F0.wireOp",EDGE,"E14.13.0.3"),sQuery(id+"F0.wireOp",EDGE,"E14.13.0.4"),sQuery(id+"F0.wireOp",EDGE,"E14.13.0.5"),sQuery(id+"F0.wireOp",EDGE,"E14.13.0.6"),sQuery(id+"F0.wireOp",EDGE,"E14.13.0.7"),sQuery(id+"F0.wireOp",EDGE,"E14.14.0.0"),sQuery(id+"F0.wireOp",EDGE,"E14.14.0.1"),sQuery(id+"F0.wireOp",EDGE,"E14.14.0.2"),sQuery(id+"F0.wireOp",EDGE,"E14.14.0.3"),sQuery(id+"F0.wireOp",EDGE,"E14.14.0.4"),sQuery(id+"F0.wireOp",EDGE,"E14.14.0.5"),sQuery(id+"F0.wireOp",EDGE,"E14.14.0.6"),sQuery(id+"F0.wireOp",EDGE,"E14.14.0.7"),sQuery(id+"F0.wireOp",EDGE,"E14.15.0.0"),sQuery(id+"F0.wireOp",EDGE,"E14.15.0.1"),sQuery(id+"F0.wireOp",EDGE,"E14.15.0.2"),sQuery(id+"F0.wireOp",EDGE,"E14.15.0.3"),sQuery(id+"F0.wireOp",EDGE,"E14.15.0.4"),sQuery(id+"F0.wireOp",EDGE,"E14.15.0.5"),sQuery(id+"F0.wireOp",EDGE,"E14.15.0.6"),sQuery(id+"F0.wireOp",EDGE,"E14.15.0.7"),sQuery(id+"F0.wireOp",EDGE,"E14.16.0.0"),sQuery(id+"F0.wireOp",EDGE,"E14.16.0.1"),sQuery(id+"F0.wireOp",EDGE,"E14.16.0.2"),sQuery(id+"F0.wireOp",EDGE,"E14.16.0.3"),sQuery(id+"F0.wireOp",EDGE,"E14.16.0.4"),sQuery(id+"F0.wireOp",EDGE,"E14.16.0.5"),sQuery(id+"F0.wireOp",EDGE,"E14.16.0.6"),sQuery(id+"F0.wireOp",EDGE,"E14.16.0.7"),sQuery(id+"F0.wireOp",EDGE,"E14.17.0.0"),sQuery(id+"F0.wireOp",EDGE,"E14.17.0.1"),sQuery(id+"F0.wireOp",EDGE,"E14.17.0.2"),sQuery(id+"F0.wireOp",EDGE,"E14.17.0.3"),sQuery(id+"F0.wireOp",EDGE,"E14.17.0.4"),sQuery(id+"F0.wireOp",EDGE,"E14.17.0.5"),sQuery(id+"F0.wireOp",EDGE,"E14.17.0.6"),sQuery(id+"F0.wireOp",EDGE,"E14.17.0.7"),sQuery(id+"F0.wireOp",EDGE,"E14.18.0.0"),sQuery(id+"F0.wireOp",EDGE,"E14.18.0.1"),sQuery(id+"F0.wireOp",EDGE,"E14.18.0.2"),sQuery(id+"F0.wireOp",EDGE,"E14.18.0.3"),sQuery(id+"F0.wireOp",EDGE,"E14.18.0.4"),sQuery(id+"F0.wireOp",EDGE,"E14.18.0.5"),sQuery(id+"F0.wireOp",EDGE,"E14.18.0.6"),sQuery(id+"F0.wireOp",EDGE,"E14.18.0.7"),sQuery(id+"F0.wireOp",EDGE,"E14.19.0.0"),sQuery(id+"F0.wireOp",EDGE,"E14.19.0.1"),sQuery(id+"F0.wireOp",EDGE,"E14.19.0.2"),sQuery(id+"F0.wireOp",EDGE,"E14.19.0.3"),sQuery(id+"F0.wireOp",EDGE,"E14.19.0.4"),sQuery(id+"F0.wireOp",EDGE,"E14.19.0.5"),sQuery(id+"F0.wireOp",EDGE,"E14.19.0.6"),sQuery(id+"F0.wireOp",EDGE,"E14.19.0.7"),sQuery(id+"F0.wireOp",EDGE,"E14.20.0.0"),sQuery(id+"F0.wireOp",EDGE,"E14.20.0.1"),sQuery(id+"F0.wireOp",EDGE,"E14.20.0.2"),sQuery(id+"F0.wireOp",EDGE,"E14.20.0.3"),sQuery(id+"F0.wireOp",EDGE,"E14.20.0.4"),sQuery(id+"F0.wireOp",EDGE,"E14.20.0.5"),sQuery(id+"F0.wireOp",EDGE,"E14.20.0.6"),sQuery(id+"F0.wireOp",EDGE,"E14.20.0.7"),sQuery(id+"F0.wireOp",EDGE,"E14.21.0.0"),sQuery(id+"F0.wireOp",EDGE,"E14.21.0.1"),sQuery(id+"F0.wireOp",EDGE,"E14.21.0.2"),sQuery(id+"F0.wireOp",EDGE,"E14.21.0.3"),sQuery(id+"F0.wireOp",EDGE,"E14.21.0.4"),sQuery(id+"F0.wireOp",EDGE,"E14.21.0.5"),sQuery(id+"F0.wireOp",EDGE,"E14.21.0.6"),sQuery(id+"F0.wireOp",EDGE,"E14.21.0.7"),sQuery(id+"F0.wireOp",EDGE,"E14.22.0.0"),sQuery(id+"F0.wireOp",EDGE,"E14.22.0.1"),sQuery(id+"F0.wireOp",EDGE,"E14.22.0.2"),sQuery(id+"F0.wireOp",EDGE,"E14.22.0.3"),sQuery(id+"F0.wireOp",EDGE,"E14.22.0.4"),sQuery(id+"F0.wireOp",EDGE,"E14.22.0.5"),sQuery(id+"F0.wireOp",EDGE,"E14.22.0.6"),sQuery(id+"F0.wireOp",EDGE,"E14.22.0.7"),sQuery(id+"F0.wireOp",EDGE,"E14.23.0.0"),sQuery(id+"F0.wireOp",EDGE,"E14.23.0.1"),sQuery(id+"F0.wireOp",EDGE,"E14.23.0.2"),sQuery(id+"F0.wireOp",EDGE,"E14.23.0.3"),sQuery(id+"F0.wireOp",EDGE,"E14.23.0.4"),sQuery(id+"F0.wireOp",EDGE,"E14.23.0.5"),sQuery(id+"F0.wireOp",EDGE,"E14.23.0.6"),sQuery(id+"F0.wireOp",EDGE,"E14.23.0.7"),sQuery(id+"F0.wireOp",EDGE,"E14.24.0.0"),sQuery(id+"F0.wireOp",EDGE,"E14.24.0.1"),sQuery(id+"F0.wireOp",EDGE,"E14.24.0.2"),sQuery(id+"F0.wireOp",EDGE,"E14.24.0.3"),sQuery(id+"F0.wireOp",EDGE,"E14.24.0.4"),sQuery(id+"F0.wireOp",EDGE,"E14.24.0.5"),sQuery(id+"F0.wireOp",EDGE,"E14.24.0.6"),sQuery(id+"F0.wireOp",EDGE,"E14.24.0.7"),sQuery(id+"F0.wireOp",EDGE,"E14.25.0.0"),sQuery(id+"F0.wireOp",EDGE,"E14.25.0.1"),sQuery(id+"F0.wireOp",EDGE,"E14.25.0.2"),sQuery(id+"F0.wireOp",EDGE,"E14.25.0.3"),sQuery(id+"F0.wireOp",EDGE,"E14.25.0.4"),sQuery(id+"F0.wireOp",EDGE,"E14.25.0.5"),sQuery(id+"F0.wireOp",EDGE,"E14.25.0.6"),sQuery(id+"F0.wireOp",EDGE,"E14.25.0.7"),sQuery(id+"F0.wireOp",EDGE,"E14.26.0.0"),sQuery(id+"F0.wireOp",EDGE,"E14.26.0.1"),sQuery(id+"F0.wireOp",EDGE,"E14.26.0.2"),sQuery(id+"F0.wireOp",EDGE,"E14.26.0.3"),sQuery(id+"F0.wireOp",EDGE,"E14.26.0.4"),sQuery(id+"F0.wireOp",EDGE,"E14.26.0.5"),sQuery(id+"F0.wireOp",EDGE,"E14.26.0.6"),sQuery(id+"F0.wireOp",EDGE,"E14.26.0.7"),sQuery(id+"F0.wireOp",EDGE,"E14.27.0.0"),sQuery(id+"F0.wireOp",EDGE,"E14.27.0.1"),sQuery(id+"F0.wireOp",EDGE,"E14.27.0.2"),sQuery(id+"F0.wireOp",EDGE,"E14.27.0.3"),sQuery(id+"F0.wireOp",EDGE,"E14.27.0.4"),sQuery(id+"F0.wireOp",EDGE,"E14.27.0.5"),sQuery(id+"F0.wireOp",EDGE,"E14.27.0.6"),sQuery(id+"F0.wireOp",EDGE,"E14.27.0.7"),sQuery(id+"F0.wireOp",EDGE,"E14.28.0.0"),sQuery(id+"F0.wireOp",EDGE,"E14.28.0.1"),sQuery(id+"F0.wireOp",EDGE,"E14.28.0.2"),sQuery(id+"F0.wireOp",EDGE,"E14.28.0.3"),sQuery(id+"F0.wireOp",EDGE,"E14.28.0.4"),sQuery(id+"F0.wireOp",EDGE,"E14.28.0.5"),sQuery(id+"F0.wireOp",EDGE,"E14.28.0.6"),sQuery(id+"F0.wireOp",EDGE,"E14.28.0.7"),sQuery(id+"F0.wireOp",EDGE,"E14.29.0.0"),sQuery(id+"F0.wireOp",EDGE,"E14.29.0.1"),sQuery(id+"F0.wireOp",EDGE,"E14.29.0.2"),sQuery(id+"F0.wireOp",EDGE,"E14.29.0.3"),sQuery(id+"F0.wireOp",EDGE,"E14.29.0.4"),sQuery(id+"F0.wireOp",EDGE,"E14.29.0.5"),sQuery(id+"F0.wireOp",EDGE,"E14.29.0.6"),sQuery(id+"F0.wireOp",EDGE,"E14.29.0.7"),sQuery(id+"F0.wireOp",EDGE,"E14.30.0.0"),sQuery(id+"F0.wireOp",EDGE,"E14.30.0.1"),sQuery(id+"F0.wireOp",EDGE,"E14.30.0.2"),sQuery(id+"F0.wireOp",EDGE,"E14.30.0.3"),sQuery(id+"F0.wireOp",EDGE,"E14.30.0.4"),sQuery(id+"F0.wireOp",EDGE,"E14.30.0.5"),sQuery(id+"F0.wireOp",EDGE,"E14.30.0.6"),sQuery(id+"F0.wireOp",EDGE,"E14.30.0.7"),sQuery(id+"F0.wireOp",EDGE,"E14.31.0.0"),sQuery(id+"F0.wireOp",EDGE,"E14.31.0.1"),sQuery(id+"F0.wireOp",EDGE,"E14.31.0.2"),sQuery(id+"F0.wireOp",EDGE,"E14.31.0.3"),sQuery(id+"F0.wireOp",EDGE,"E14.31.0.4"),sQuery(id+"F0.wireOp",EDGE,"E14.31.0.5"),sQuery(id+"F0.wireOp",EDGE,"E14.31.0.6"),sQuery(id+"F0.wireOp",EDGE,"E14.31.0.7"),sQuery(id+"F0.wireOp",EDGE,"E14.32.0.0"),sQuery(id+"F0.wireOp",EDGE,"E14.32.0.1"),sQuery(id+"F0.wireOp",EDGE,"E14.32.0.2"),sQuery(id+"F0.wireOp",EDGE,"E14.32.0.3"),sQuery(id+"F0.wireOp",EDGE,"E14.32.0.4"),sQuery(id+"F0.wireOp",EDGE,"E14.32.0.5"),sQuery(id+"F0.wireOp",EDGE,"E14.32.0.6"),sQuery(id+"F0.wireOp",EDGE,"E14.32.0.7"),sQuery(id+"F0.wireOp",EDGE,"E14.33.0.0"),sQuery(id+"F0.wireOp",EDGE,"E14.33.0.1"),sQuery(id+"F0.wireOp",EDGE,"E14.33.0.2"),sQuery(id+"F0.wireOp",EDGE,"E14.33.0.3"),sQuery(id+"F0.wireOp",EDGE,"E14.33.0.4"),sQuery(id+"F0.wireOp",EDGE,"E14.33.0.5"),sQuery(id+"F0.wireOp",EDGE,"E14.33.0.6"),sQuery(id+"F0.wireOp",EDGE,"E14.33.0.7"),sQuery(id+"F0.wireOp",EDGE,"E14.34.0.0"),sQuery(id+"F0.wireOp",EDGE,"E14.34.0.1"),sQuery(id+"F0.wireOp",EDGE,"E14.34.0.2"),sQuery(id+"F0.wireOp",EDGE,"E14.34.0.3"),sQuery(id+"F0.wireOp",EDGE,"E14.34.0.4"),sQuery(id+"F0.wireOp",EDGE,"E14.34.0.5"),sQuery(id+"F0.wireOp",EDGE,"E14.34.0.6"),sQuery(id+"F0.wireOp",EDGE,"E14.34.0.7"),sQuery(id+"F0.wireOp",EDGE,"E14.35.0.0"),sQuery(id+"F0.wireOp",EDGE,"E14.35.0.1"),sQuery(id+"F0.wireOp",EDGE,"E14.35.0.2"),sQuery(id+"F0.wireOp",EDGE,"E14.35.0.3"),sQuery(id+"F0.wireOp",EDGE,"E14.35.0.4"),sQuery(id+"F0.wireOp",EDGE,"E14.35.0.5"),sQuery(id+"F0.wireOp",EDGE,"E14.35.0.6"),sQuery(id+"F0.wireOp",EDGE,"E14.35.0.7"),sQuery(id+"F0.wireOp",EDGE,"E14.36.0.0"),sQuery(id+"F0.wireOp",EDGE,"E14.36.0.1"),sQuery(id+"F0.wireOp",EDGE,"E14.36.0.2"),sQuery(id+"F0.wireOp",EDGE,"E14.36.0.3"),sQuery(id+"F0.wireOp",EDGE,"E14.36.0.4"),sQuery(id+"F0.wireOp",EDGE,"E14.36.0.5"),sQuery(id+"F0.wireOp",EDGE,"E14.36.0.6"),sQuery(id+"F0.wireOp",EDGE,"E14.36.0.7"),sQuery(id+"F0.wireOp",EDGE,"E14.37.0.0"),sQuery(id+"F0.wireOp",EDGE,"E14.37.0.1"),sQuery(id+"F0.wireOp",EDGE,"E14.37.0.2"),sQuery(id+"F0.wireOp",EDGE,"E14.37.0.3"),sQuery(id+"F0.wireOp",EDGE,"E14.37.0.4"),sQuery(id+"F0.wireOp",EDGE,"E14.37.0.5"),sQuery(id+"F0.wireOp",EDGE,"E14.37.0.6"),sQuery(id+"F0.wireOp",EDGE,"E14.37.0.7"),sQuery(id+"F0.wireOp",EDGE,"E14.38.0.0"),sQuery(id+"F0.wireOp",EDGE,"E14.38.0.1"),sQuery(id+"F0.wireOp",EDGE,"E14.38.0.2"),sQuery(id+"F0.wireOp",EDGE,"E14.38.0.3"),sQuery(id+"F0.wireOp",EDGE,"E14.38.0.4"),sQuery(id+"F0.wireOp",EDGE,"E14.38.0.5"),sQuery(id+"F0.wireOp",EDGE,"E14.38.0.6"),sQuery(id+"F0.wireOp",EDGE,"E14.38.0.7"),sQuery(id+"F0.wireOp",EDGE,"E14.39.0.0"),sQuery(id+"F0.wireOp",EDGE,"E14.39.0.1"),sQuery(id+"F0.wireOp",EDGE,"E14.39.0.2"),sQuery(id+"F0.wireOp",EDGE,"E14.39.0.3"),sQuery(id+"F0.wireOp",EDGE,"E14.39.0.4"),sQuery(id+"F0.wireOp",EDGE,"E14.39.0.5"),sQuery(id+"F0.wireOp",EDGE,"E14.39.0.6"),sQuery(id+"F0.wireOp",EDGE,"E14.39.0.7"),sQuery(id+"F0.wireOp",EDGE,"E14.40.0.0"),sQuery(id+"F0.wireOp",EDGE,"E14.40.0.1"),sQuery(id+"F0.wireOp",EDGE,"E14.40.0.2"),sQuery(id+"F0.wireOp",EDGE,"E14.40.0.3"),sQuery(id+"F0.wireOp",EDGE,"E14.40.0.4"),sQuery(id+"F0.wireOp",EDGE,"E14.40.0.5"),sQuery(id+"F0.wireOp",EDGE,"E14.40.0.6"),sQuery(id+"F0.wireOp",EDGE,"E14.40.0.7"),sQuery(id+"F0.wireOp",EDGE,"E14.41.0.0"),sQuery(id+"F0.wireOp",EDGE,"E14.41.0.1"),sQuery(id+"F0.wireOp",EDGE,"E14.41.0.2"),sQuery(id+"F0.wireOp",EDGE,"E14.41.0.3"),sQuery(id+"F0.wireOp",EDGE,"E14.41.0.4"),sQuery(id+"F0.wireOp",EDGE,"E14.41.0.5"),sQuery(id+"F0.wireOp",EDGE,"E14.41.0.6"),sQuery(id+"F0.wireOp",EDGE,"E14.41.0.7"),sQuery(id+"F0.wireOp",EDGE,"E14.42.0.0"),sQuery(id+"F0.wireOp",EDGE,"E14.42.0.1"),sQuery(id+"F0.wireOp",EDGE,"E14.42.0.2"),sQuery(id+"F0.wireOp",EDGE,"E14.42.0.3"),sQuery(id+"F0.wireOp",EDGE,"E14.42.0.4"),sQuery(id+"F0.wireOp",EDGE,"E14.42.0.5"),sQuery(id+"F0.wireOp",EDGE,"E14.42.0.6"),sQuery(id+"F0.wireOp",EDGE,"E14.42.0.7"),sQuery(id+"F0.wireOp",EDGE,"E14.43.0.0"),sQuery(id+"F0.wireOp",EDGE,"E14.43.0.1"),sQuery(id+"F0.wireOp",EDGE,"E14.43.0.2"),sQuery(id+"F0.wireOp",EDGE,"E14.43.0.3"),sQuery(id+"F0.wireOp",EDGE,"E14.43.0.4"),sQuery(id+"F0.wireOp",EDGE,"E14.43.0.5"),sQuery(id+"F0.wireOp",EDGE,"E14.43.0.6"),sQuery(id+"F0.wireOp",EDGE,"E14.43.0.7"),sQuery(id+"F0.wireOp",EDGE,"E14.44.0.0"),sQuery(id+"F0.wireOp",EDGE,"E14.44.0.1"),sQuery(id+"F0.wireOp",EDGE,"E14.44.0.2"),sQuery(id+"F0.wireOp",EDGE,"E14.44.0.3"),sQuery(id+"F0.wireOp",EDGE,"E14.44.0.4"),sQuery(id+"F0.wireOp",EDGE,"E14.44.0.5"),sQuery(id+"F0.wireOp",EDGE,"E14.44.0.6"),sQuery(id+"F0.wireOp",EDGE,"E14.44.0.7"),sQuery(id+"F0.wireOp",EDGE,"E14.45.0.0"),sQuery(id+"F0.wireOp",EDGE,"E14.45.0.1"),sQuery(id+"F0.wireOp",EDGE,"E14.45.0.2"),sQuery(id+"F0.wireOp",EDGE,"E14.45.0.3"),sQuery(id+"F0.wireOp",EDGE,"E14.45.0.4"),sQuery(id+"F0.wireOp",EDGE,"E14.45.0.5"),sQuery(id+"F0.wireOp",EDGE,"E14.45.0.6"),sQuery(id+"F0.wireOp",EDGE,"E14.45.0.7"),sQuery(id+"F0.wireOp",EDGE,"E14.46.0.0"),sQuery(id+"F0.wireOp",EDGE,"E14.46.0.1"),sQuery(id+"F0.wireOp",EDGE,"E14.46.0.2"),sQuery(id+"F0.wireOp",EDGE,"E14.46.0.3"),sQuery(id+"F0.wireOp",EDGE,"E14.46.0.4"),sQuery(id+"F0.wireOp",EDGE,"E14.46.0.5"),sQuery(id+"F0.wireOp",EDGE,"E14.46.0.6"),sQuery(id+"F0.wireOp",EDGE,"E14.46.0.7"),sQuery(id+"F0.wireOp",EDGE,"E14.47.0.0"),sQuery(id+"F0.wireOp",EDGE,"E14.47.0.1"),sQuery(id+"F0.wireOp",EDGE,"E14.47.0.2"),sQuery(id+"F0.wireOp",EDGE,"E14.47.0.3"),sQuery(id+"F0.wireOp",EDGE,"E14.47.0.4"),sQuery(id+"F0.wireOp",EDGE,"E14.47.0.5"),sQuery(id+"F0.wireOp",EDGE,"E14.47.0.6"),sQuery(id+"F0.wireOp",EDGE,"E14.47.0.7"),sQuery(id+"F0.wireOp",EDGE,"E14.48.0.0"),sQuery(id+"F0.wireOp",EDGE,"E14.48.0.1"),sQuery(id+"F0.wireOp",EDGE,"E14.48.0.2"),sQuery(id+"F0.wireOp",EDGE,"E14.48.0.3"),sQuery(id+"F0.wireOp",EDGE,"E14.48.0.4"),sQuery(id+"F0.wireOp",EDGE,"E14.48.0.5"),sQuery(id+"F0.wireOp",EDGE,"E14.48.0.6"),sQuery(id+"F0.wireOp",EDGE,"E14.48.0.7"),sQuery(id+"F0.wireOp",EDGE,"E14.49.0.0"),sQuery(id+"F0.wireOp",EDGE,"E14.49.0.1"),sQuery(id+"F0.wireOp",EDGE,"E14.49.0.2"),sQuery(id+"F0.wireOp",EDGE,"E14.49.0.3"),sQuery(id+"F0.wireOp",EDGE,"E14.49.0.4"),sQuery(id+"F0.wireOp",EDGE,"E14.49.0.5"),sQuery(id+"F0.wireOp",EDGE,"E14.49.0.6"),sQuery(id+"F0.wireOp",EDGE,"E14.49.0.7")])]});
            hole(context, id + "F8", {"style" : HoleStyle.SIMPLE, "endStyle" : HoleEndStyle.THROUGH, "holeDiameter" : 6.35 * mm, "tappedDepth" : 12.7 * mm, "tapClearance" : 3, "locations" : qUnion([Q0, Q1, Q2, Q3, Q4, Q5, Q6, Q7]), "scope" : qUnion([Q8])});
        }
    });
